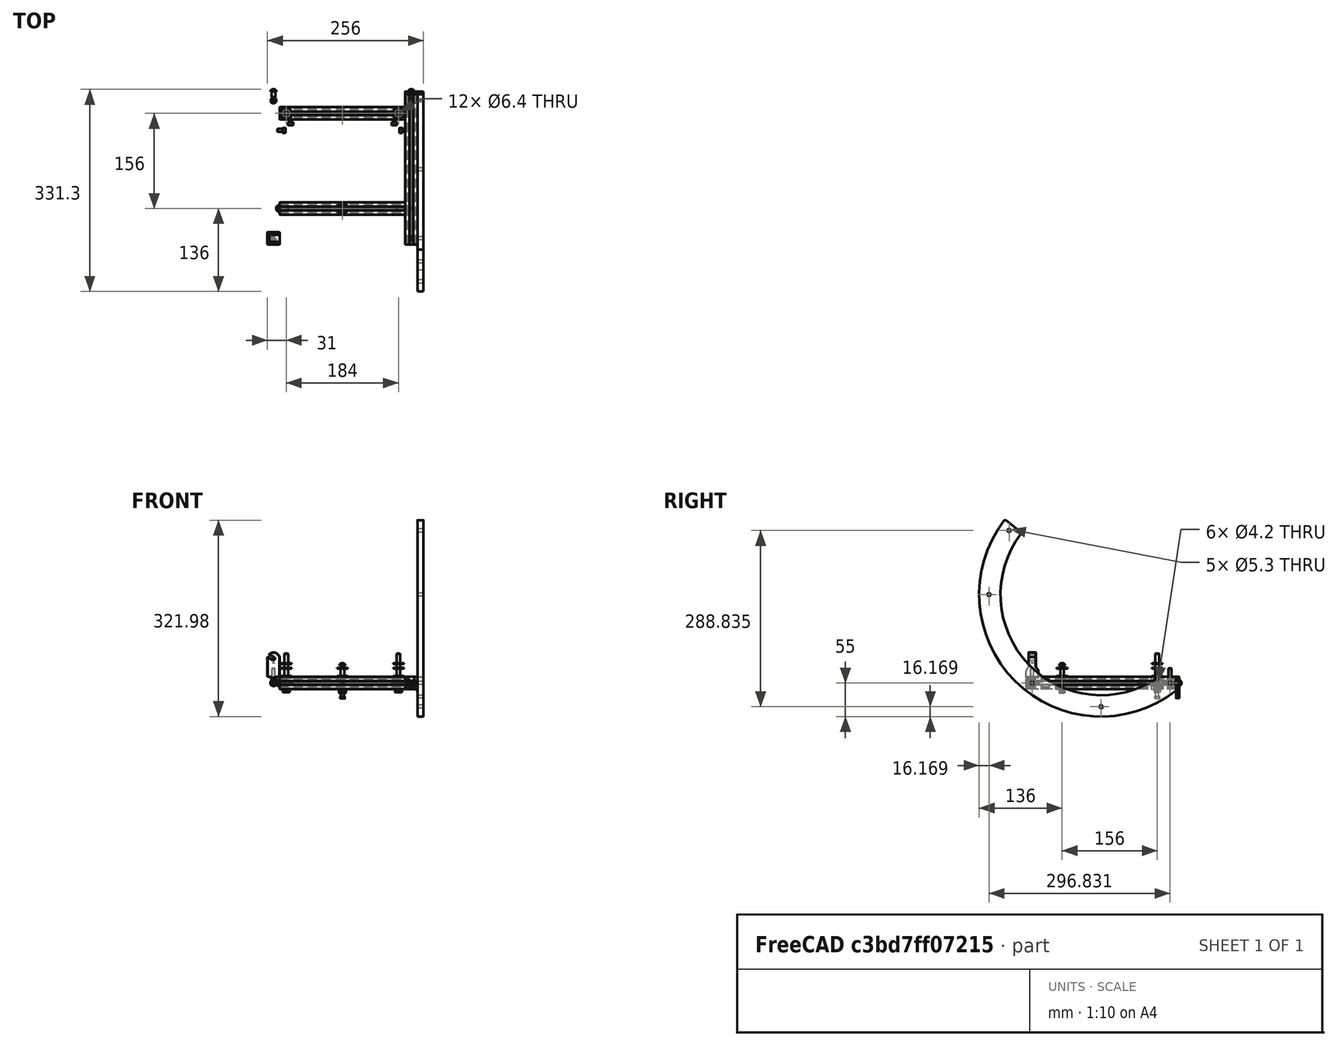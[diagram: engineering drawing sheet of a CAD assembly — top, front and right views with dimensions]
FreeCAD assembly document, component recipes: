
FREECAD ASSEMBLY — COMPONENT RECIPES ("Primary")

This assembly document has 7 components, labeled P0..P6 below (a component is one placed body or linked part). 6 of them carry a construction recipe — the FreeCAD feature program that regenerates the part from scratch, quoted from this document or its linked companion documents; the rest are supplied as boundary geometry only. No exploded tour is included for this assembly.
COMPONENT P0 — geometry summary ("EndStopper_M"; no construction recipe available for this part):
  bounding box: 35.0 x 30.0 x 10.0 mm
  tessellated surface: 1,512 triangles
  volume: 3951 mm^3 (38% of its bounding box)
COMPONENT P1 — recipe-attached ("RockerRail", modeled in this document).
Construction recipe (the document's own serialized feature program — sketch geometry with constraints, then the solid features built on it; lengths are millimeters unless a unit is written):

FEATURE [Sketcher::SketchObject] Sketch004  label="RockerRail_Base_Sketch"
  FullyConstrained = true
  MapMode = 5
  Placement = pos=(0,0,0) rot=(0.57735,0.57735,0.57735;2.0944rad)
  Support = -> [YZ_Plane011]
  expr: Constraints[12] = <<Common>>#<<Parameters>>.bolt_y - 10
  expr: Constraints[19] = <<Common>>#<<Parameters>>.pri_fillet
  expr: Constraints[1] = <<Common>>#<<Parameters>>.rail_dia
  expr: Constraints[35] = <<Common>>#<<Parameters>>.rail_dia - <<Common>>#<<Parameters>>.rail_height * 2
  expr: Constraints[36] = <<Common>>#<<Parameters>>.datum_lowercell - <<Common>>#<<Parameters>>.datum_rocker_z + 10
  expr: Constraints[40] = <<Common>>#<<Parameters>>.boxsize_y
  expr: Constraints[8] = <<Common>>#<<Parameters>>.boxsize_y
  sketch-geometry (16):
    g0: ArcOfCircle CenterX=0 CenterY=0 CenterZ=0 NormalX=0 NormalY=0 NormalZ=1 AngleXU=0 Radius=200 StartAngle=2.49187 EndAngle=5.36861
    g1: Circle CenterX=0 CenterY=0 CenterZ=0 NormalX=0 NormalY=0 NormalZ=1 AngleXU=0 Radius=165
    g2: LineSegment StartX=-155.722 StartY=121.453 StartZ=0 EndX=-132.064 EndY=103.001 EndZ=0
    g3: ArcOfCircle CenterX=0 CenterY=0 CenterZ=0 NormalX=0 NormalY=0 NormalZ=1 AngleXU=0 Radius=165 StartAngle=2.49413 EndAngle=5.32021
    g4: LineSegment StartX=95.6556 StartY=-135 StartZ=0 EndX=120.5 EndY=-135 EndZ=0
    g5: LineSegment StartX=123 StartY=-156.48 StartZ=0 EndX=123 EndY=-137.5 EndZ=0
    g6: LineSegment StartX=-123 StartY=-157.705 StartZ=0 EndX=123 EndY=-157.705 EndZ=0
    g7: LineSegment StartX=103 StartY=-157.705 StartZ=0 EndX=103 EndY=-128.903 EndZ=0
    g8: LineSegment StartX=0 StartY=0 StartZ=0 EndX=123 EndY=-135 EndZ=0
    g9: ArcOfCircle CenterX=120.5 CenterY=-137.5 CenterZ=0 NormalX=0 NormalY=0 NormalZ=1 AngleXU=0 Radius=2.5 StartAngle=-1.8e-15 EndAngle=1.5708
    g10: GeomPoint X=123 Y=-135 Z=0
    g11: ArcOfCircle CenterX=120.5 CenterY=-156.48 CenterZ=0 NormalX=0 NormalY=0 NormalZ=1 AngleXU=0 Radius=2.5 StartAngle=5.36861 EndAngle=6.28319
    g12: ArcOfCircle CenterX=-157.259 CenterY=119.481 CenterZ=0 NormalX=0 NormalY=0 NormalZ=1 AngleXU=0 Radius=2.5 StartAngle=0.90841 EndAngle=2.49187
    g13: ArcOfCircle CenterX=-133.601 CenterY=101.03 CenterZ=0 NormalX=0 NormalY=0 NormalZ=1 AngleXU=0 Radius=2.5 StartAngle=5.63573 EndAngle=7.1916
    g14: ArcOfCircle CenterX=95.6556 CenterY=-137.5 CenterZ=0 NormalX=0 NormalY=0 NormalZ=1 AngleXU=0 Radius=2.5 StartAngle=1.5708 EndAngle=2.17862
    g15: LineSegment StartX=-157.705 StartY=123 StartZ=0 EndX=-157.705 EndY=-123 EndZ=0
  constraints (42):
    c: Coincident(g0,g-1)
    c: Diameter(g0) = 400
    c: Coincident(g1,g0)
    c: PointOnObject(g0,g2)
    c: Coincident(g3,g0)
    c: Horizontal(g4)
    c: Vertical(g5)
    c: Symmetric(g6,g6,g-2)
    c: DistanceX(g6,g6) = 246
    c: PointOnObject(g7,g6)
    c: Vertical(g7)
    c: PointOnObject(g7,g1)
    c: DistanceX(g7) = 103
    c: Coincident(g8,g0)
    c: Coincident(g8,g10)
    c: PointOnObject(g10,g4)
    c: PointOnObject(g10,g5)
    c: Tangent(g4,g9) = 1.5708
    c: Tangent(g5,g9) = -1.5708
    c: Radius(g9) = 2.5
    c: Tangent(g5,g11) = -1.5708
    c: Tangent(g0,g11) = -1.5708
    c: Equal(g11,g9)
    c: PointOnObject(g6,g5)
    c: Tangent(g2,g12) = 1.5708
    c: Tangent(g0,g12) = -1.5708
    c: Equal(g12,g9)
    c: Tangent(g2,g13) = 1.5708
    c: Tangent(g3,g13) = 1.5708
    c: Equal(g12,g13)
    c: PointOnObject(g3,g1)
    c: Tangent(g4,g14) = 1.5708
    c: Tangent(g3,g14) = 1.5708
    c: Equal(g14,g9)
    c: PointOnObject(g6,g0)
    c: Diameter(g1) = 330
    c: DistanceY(g4) = -135
    c: PointOnObject(g15,g0)
    c: PointOnObject(g15,g0)
    c: Vertical(g15)
    c: DistanceY(g15,g15) = 246
    c: PointOnObject(g15,g2)
FEATURE [PartDesign::Plane] DatumPlane  label="DatumPlane_RockerBase_OuterFace"
  AttachmentOffset = pos=(0,0,5) rot=(0,0,1;0rad)
  Length = 386.928
  MapMode = 5
  Placement = pos=(5,-1.1e-15,1.1e-15) rot=(0.57735,0.57735,0.57735;2.0944rad)
  ResizeMode = 0
  Support = -> [YZ_Plane011]
  Width = 385.995
  expr: .AttachmentOffset.Base.z = <<Common>>#<<Parameters>>.rail_width / 2
FEATURE [PartDesign::Pad] Pad008  label="RockerRail_Base"
  Direction = (1,-2e-16,3e-16)
  Length = 10
  Length2 = 100
  Midplane = true
  Placement = pos=(0,0,0) rot=(0.57735,0.57735,0.57735;2.0944rad)
  Profile = -> Sketch004
  Type = 0
  expr: Length = <<Common>>#<<Parameters>>.rail_width
FEATURE [Sketcher::SketchObject] Sketch007  label="RockerRail_MountHoles_Sketch"
  ExternalGeometry = -> [Pad008]
  FullyConstrained = true
  MapMode = 5
  Placement = pos=(5,-1.1e-15,1.1e-15) rot=(0.57735,0.57735,0.57735;2.0944rad)
  Support = -> [DatumPlane]
  expr: Constraints[1] = <<Common>>#<<Parameters>>.bolt_y
  expr: Constraints[6] = <<Common>>#<<Parameters>>.datum_lowercell - <<Common>>#<<Parameters>>.datum_rocker_z
  sketch-geometry (8):
    g0: LineSegment StartX=-113 StartY=-145 StartZ=0 EndX=113 EndY=-145 EndZ=0
    g1: Circle CenterX=-113 CenterY=-145 CenterZ=0 NormalX=0 NormalY=0 NormalZ=1 AngleXU=0 Radius=2.5
    g2: Circle CenterX=113 CenterY=-145 CenterZ=0 NormalX=0 NormalY=0 NormalZ=1 AngleXU=0 Radius=2.5
    g3: Circle CenterX=0 CenterY=0 CenterZ=0 NormalX=0 NormalY=0 NormalZ=1 AngleXU=0 Radius=183.831
    g4: Circle CenterX=-150.891 CenterY=105.004 CenterZ=0 NormalX=0 NormalY=0 NormalZ=1 AngleXU=0 Radius=10
    g5: Circle CenterX=0 CenterY=-183.831 CenterZ=0 NormalX=0 NormalY=0 NormalZ=1 AngleXU=0 Radius=2.5
    g6: Circle CenterX=-183.831 CenterY=0 CenterZ=0 NormalX=0 NormalY=0 NormalZ=1 AngleXU=0 Radius=2.5
    g7: Circle CenterX=-150.891 CenterY=105.004 CenterZ=0 NormalX=0 NormalY=0 NormalZ=1 AngleXU=0 Radius=2.5
  constraints (22):
    c: Symmetric(g0,g0,g-2)
    c: DistanceX(g0) = 113
    c: Coincident(g1,g0)
    c: Coincident(g2,g0)
    c: Diameter(g2) = 5
    c: Equal(g2,g1)
    c: DistanceY(g2) = -145
    c: Distance(g-1,g1) = 183.831
    c: Coincident(g3,g-1)
    c: PointOnObject(g0,g3)
    c: PointOnObject(g4,g3)
    c: Tangent(g4,g-3)
    c: Radius(g4) = 10
    c: PointOnObject(g5,g-2)
    c: PointOnObject(g6,g3)
    c: Coincident(g7,g4)
    c: Equal(g7,g6)
    c: Equal(g6,g5)
    c: Equal(g5,g2)
    c: PointOnObject(g6,g-1)
    c: PointOnObject(g5,g3)
    c: Radius(g3) = 183.831
FEATURE [PartDesign::Hole] Hole003  label="RockerRail_MountHoles"
  BaseFeature = -> Pad008
  CustomThreadClearance = 0
  Depth = 25
  DepthType = 1
  Diameter = 5.3
  DrillForDepth = false
  DrillPoint = 1
  DrillPointAngle = 118
  HoleCutCountersinkAngle = 90
  HoleCutCustomValues = false
  HoleCutDepth = 0
  HoleCutDiameter = 12.2
  HoleCutType = 0
  ModelThread = false
  Placement = pos=(0,0,0) rot=(0.57735,0.57735,0.57735;2.0944rad)
  Profile = -> Sketch007
  Tapered = false
  TaperedAngle = 90
  ThreadClass = 0
  ThreadDepth = 23.5
  ThreadDepthType = 0
  ThreadDirection = 0
  ThreadFit = 1
  ThreadSize = 13
  ThreadType = 1
  Threaded = false
  UseCustomThreadClearance = false
FEATURE [PartDesign::CoordinateSystem] Local_CS024  label="LCS_RockerBolt_AS"
  AttacherType = Attacher::AttachEngine3D
  MapMode = 11
  Placement = pos=(-5,113,-145) rot=(0.707107,0,-0.707107;3.14159rad)
  Support = -> [Hole003]
FEATURE [PartDesign::CoordinateSystem] Local_CS026  label="LCS_RockerBolt_FS"
  AttacherType = Attacher::AttachEngine3D
  MapMode = 11
  Placement = pos=(-5,-113,-145) rot=(0.707107,0,-0.707107;3.14159rad)
  Support = -> [Hole003]
FEATURE [PartDesign::CoordinateSystem] Local_CS028  label="LCS_RockerBolt_AP"
  AttacherType = Attacher::AttachEngine3D
  MapMode = 11
  Placement = pos=(5,113,-145) rot=(0.707107,0,0.707107;3.14159rad)
  Support = -> [Hole003]
FEATURE [PartDesign::CoordinateSystem] Local_CS030  label="LCS_RockerBolt_FP"
  AttacherType = Attacher::AttachEngine3D
  MapMode = 11
  Placement = pos=(5,-113,-145) rot=(0.707107,0,0.707107;3.14159rad)
  Support = -> [Hole003]
FEATURE [PartDesign::Body] Body006  label="RockerRail"
  Group = -> [Sketch004,Sketch007,DatumPlane,Pad008,Hole003,Local_CS024,Local_CS026,Local_CS028,Local_CS030]
  Origin = -> Origin011
  Placement = pos=(128,0,83) rot=(0,0,1;0rad)
  Tip = -> Hole003
  expr: .Placement.Base.x = <<Common>>#<<Parameters>>.boxsize_x / 2 + <<Common>>#<<Parameters>>.rail_width / 2
  expr: .Placement.Base.z = <<Common>>#<<Parameters>>.datum_rocker_z
COMPONENT P2 — recipe-attached ("SideArmBase", modeled in this document).
Construction recipe (the document's own serialized feature program — sketch geometry with constraints, then the solid features built on it; lengths are millimeters unless a unit is written):

FEATURE [Sketcher::SketchObject] Sketch187  label="FrameBase_InnerCut_Sketch"
  AttachmentOffset = pos=(0,0,30) rot=(0,0,1;0rad)
  FullyConstrained = true
  MapMode = 5
  Placement = pos=(0,0,30) rot=(0,0,1;0rad)
  Support = -> [XY_Plane091]
  expr: .AttachmentOffset.Base.z = <<Common>>#<<Parameters>>.pri_braceriser
  sketch-geometry (1):
    g0: Circle CenterX=0 CenterY=0 CenterZ=0 NormalX=0 NormalY=0 NormalZ=1 AngleXU=0 Radius=4.75
  constraints (2):
    c: Diameter(g0) = 9.5
    c: Coincident(g0,g-1)
FEATURE [Sketcher::SketchObject] Sketch188  label="FrameBase_MountBolt_Sketch"
  AttachmentOffset = pos=(0,0,2) rot=(0,0,1;0rad)
  FullyConstrained = true
  MapMode = 5
  Placement = pos=(0,0,-2) rot=(0,1,0;3.14159rad)
  Support = -> [XY_Plane091]
  sketch-geometry (1):
    g0: Circle CenterX=0 CenterY=0 CenterZ=0 NormalX=0 NormalY=0 NormalZ=1 AngleXU=0 Radius=2.5
  constraints (2):
    c: Diameter(g0) = 5
    c: Coincident(g0,g-1)
FEATURE [Sketcher::SketchObject] Sketch189  label="FrameBase_Pivot_Sketch"
  FullyConstrained = true
  MapMode = 5
  Placement = pos=(0,0,0) rot=(1,0,0;1.5708rad)
  Support = -> [XZ_Plane092]
  expr: Constraints[10] = <<Common>>#<<Parameters>>.sec_sidebolt * 1.1
  expr: Constraints[4] = <<Common>>#<<Parameters>>.pri_bracepivotdia
  expr: Constraints[5] = <<Common>>#<<Parameters>>.pri_braceriser
  sketch-geometry (15):
    g0: LineSegment StartX=-10 StartY=0 StartZ=0 EndX=-10 EndY=30 EndZ=0
    g1: LineSegment StartX=10 StartY=0 StartZ=0 EndX=10 EndY=32.6795 EndZ=0
    g2: ArcOfCircle CenterX=0 CenterY=30 CenterZ=0 NormalX=0 NormalY=0 NormalZ=1 AngleXU=0 Radius=10 StartAngle=0.523599 EndAngle=2.39618
    g3: ArcOfCircle CenterX=0 CenterY=30 CenterZ=0 NormalX=0 NormalY=0 NormalZ=1 AngleXU=0 Radius=2.2 StartAngle=4.18879 EndAngle=7.33038
    g4: LineSegment StartX=-7.34808 StartY=36.7828 StartZ=0 EndX=1.1 EndY=31.9053 EndZ=0
    g5: LineSegment StartX=-1.1 StartY=28.0947 StartZ=0 EndX=-9.54808 EndY=32.9722 EndZ=0
    g6: LineSegment StartX=1.1 StartY=31.9053 StartZ=0 EndX=-1.1 EndY=28.0947 EndZ=0
    g7: ArcOfCircle CenterX=0 CenterY=30 CenterZ=0 NormalX=0 NormalY=0 NormalZ=1 AngleXU=0 Radius=10 StartAngle=2.83981 EndAngle=3.14159
    g8: LineSegment StartX=-10 StartY=30 StartZ=0 EndX=10 EndY=30 EndZ=0
    g9: LineSegment StartX=-10 StartY=0 StartZ=0 EndX=-3 EndY=0 EndZ=0
    g10: LineSegment StartX=10 StartY=0 StartZ=0 EndX=3 EndY=0 EndZ=0
    g11: LineSegment StartX=3 StartY=0 StartZ=0 EndX=1.8453 EndY=-2 EndZ=0
    g12: LineSegment StartX=1.8453 StartY=-2 StartZ=0 EndX=-3 EndY=-2 EndZ=0
    g13: LineSegment StartX=-3 StartY=-2 StartZ=0 EndX=-3 EndY=0 EndZ=0
    g14: LineSegment StartX=8.66025 StartY=35 StartZ=0 EndX=10 EndY=32.6795 EndZ=0
  constraints (42):
    c: PointOnObject(g1,g-1)
    c: Vertical(g0)
    c: Vertical(g1)
    c: PointOnObject(g2,g-2)
    c: Diameter(g2) = 20
    c: DistanceY(g2) = 30
    c: Coincident(g3,g2)
    c: Coincident(g4,g2)
    c: Coincident(g4,g3)
    c: Coincident(g5,g3)
    c: Diameter(g3) = 4.4
    c: Symmetric(g1,g0,g-2)
    c: Coincident(g6,g3)
    c: Coincident(g6,g3)
    c: PointOnObject(g2,g6)
    c: Parallel(g5,g4)
    c: Coincident(g7,g2)
    c: Coincident(g7,g5)
    c: Coincident(g7,g0)
    c: Coincident(g8,g0)
    c: PointOnObject(g2,g8)
    c: Perpendicular(g4,g6)
    c: Horizontal(g8)
    c: Angle(g4,g8) = 0.523599
    c: Coincident(g9,g0)
    c: Horizontal(g9)
    c: Coincident(g10,g1)
    c: Coincident(g11,g10)
    c: Coincident(g12,g11)
    c: Horizontal(g12)
    c: Coincident(g13,g12)
    c: Coincident(g13,g9)
    c: Vertical(g13)
    c: DistanceX(g9,g10) = 6
    c: Symmetric(g10,g9,g-2)
    c: DistanceY(g13,g13) = 2
    c: Angle(g11,g10) = 2.0944
    c: PointOnObject(g8,g1)
    c: DistanceX(g1) = 10
    c: Coincident(g14,g1)
    c: Tangent(g14,g2) = 1.5708
    c: Angle(g14,g1) = 2.61799
FEATURE [Sketcher::SketchObject] Sketch190  label="FrameBase_Hinge_Sketch"
  FullyConstrained = true
  MapMode = 5
  Placement = pos=(0,0,0) rot=(0.57735,0.57735,0.57735;2.0944rad)
  Support = -> [YZ_Plane092]
  expr: Constraints[22] = <<Common>>#<<Parameters>>.pri_braceriser + <<Common>>#<<Parameters>>.pri_bracepivotdia / 2
  expr: Constraints[23] = <<Common>>#<<Parameters>>.pri_braceriser + <<Common>>#<<Parameters>>.pri_bracepivotdia / 2 + 1
  expr: Constraints[26] = <<Common>>#<<Parameters>>.pri_braceriser - <<Common>>#<<Parameters>>.pri_bracepivotdia / 2 - <<Common>>#<<Parameters>>.sec_fthick / 2
  expr: Constraints[35] = <<Common>>#<<Parameters>>.sec_fthick + 1
  expr: Constraints[47] = <<Common>>#<<Parameters>>.sec_fthick * 2
  expr: Constraints[4] = <<Common>>#<<Parameters>>.sec_fthick
  sketch-geometry (20):
    g0: LineSegment StartX=6 StartY=18.5 StartZ=0 EndX=6 EndY=40 EndZ=0
    g1: LineSegment StartX=6 StartY=40 StartZ=0 EndX=-6 EndY=40 EndZ=0
    g2: LineSegment StartX=-6 StartY=40 StartZ=0 EndX=-6 EndY=18.5 EndZ=0
    g3: LineSegment StartX=-10 StartY=3 StartZ=0 EndX=10 EndY=3 EndZ=0
    g4: LineSegment StartX=10 StartY=9.55573 StartZ=0 EndX=10 EndY=3 EndZ=0
    g5: LineSegment StartX=-10 StartY=9.55573 StartZ=0 EndX=-10 EndY=3 EndZ=0
    g6: LineSegment StartX=10 StartY=3 StartZ=0 EndX=11 EndY=3 EndZ=0
    g7: LineSegment StartX=11 StartY=3 StartZ=0 EndX=11 EndY=41 EndZ=0
    g8: LineSegment StartX=-10 StartY=3 StartZ=0 EndX=-11 EndY=3 EndZ=0
    g9: LineSegment StartX=-11 StartY=3 StartZ=0 EndX=-11 EndY=41 EndZ=0
    g10: LineSegment StartX=-11 StartY=41 StartZ=0 EndX=11 EndY=41 EndZ=0
    g11: LineSegment StartX=-6 StartY=18.5 StartZ=0 EndX=6 EndY=18.5 EndZ=0
    g12: LineSegment StartX=6 StartY=18.5 StartZ=0 EndX=10 EndY=18.5 EndZ=0
    g13: LineSegment StartX=-6 StartY=18.5 StartZ=0 EndX=-10 EndY=18.5 EndZ=0
    g14: ArcOfCircle CenterX=-12 CenterY=18.5 CenterZ=0 NormalX=0 NormalY=0 NormalZ=1 AngleXU=0 Radius=6 StartAngle=5.44212 EndAngle=6.28319
    g15: ArcOfCircle CenterX=-4 CenterY=9.55573 CenterZ=0 NormalX=0 NormalY=0 NormalZ=1 AngleXU=0 Radius=6 StartAngle=2.30052 EndAngle=3.14159
    g16: ArcOfCircle CenterX=12 CenterY=18.5 CenterZ=0 NormalX=0 NormalY=0 NormalZ=1 AngleXU=0 Radius=6 StartAngle=3.14159 EndAngle=3.98266
    g17: ArcOfCircle CenterX=4 CenterY=9.55573 CenterZ=0 NormalX=0 NormalY=0 NormalZ=1 AngleXU=0 Radius=6 StartAngle=1e-16 EndAngle=0.841069
    g18: LineSegment StartX=-12 StartY=18.5 StartZ=0 EndX=-4 EndY=9.55573 EndZ=0
    g19: LineSegment StartX=4 StartY=9.55573 StartZ=0 EndX=12 EndY=18.5 EndZ=0
  constraints (55):
    c: Coincident(g1,g0)
    c: Coincident(g2,g1)
    c: Vertical(g2)
    c: Symmetric(g3,g3,g-2)
    c: DistanceY(g-1,g3) = 3
    c: DistanceX(g3,g3) = 20
    c: Vertical(g0)
    c: Symmetric(g1,g0,g-2)
    c: Coincident(g4,g3)
    c: Coincident(g5,g3)
    c: Coincident(g6,g4)
    c: Coincident(g7,g6)
    c: Vertical(g7)
    c: Coincident(g8,g5)
    c: Horizontal(g8)
    c: Coincident(g9,g8)
    c: Vertical(g9)
    c: Coincident(g10,g9)
    c: Coincident(g10,g7)
    c: Symmetric(g7,g9,g-2)
    c: DistanceX(g6,g6) = 1
    c: Horizontal(g6)
    c: DistanceY(g1) = 40
    c: DistanceY(g7) = 41
    c: Coincident(g11,g2)
    c: Horizontal(g11)
    c: DistanceY(g2) = 18.5
    c: Vertical(g4)
    c: Vertical(g5)
    c: Coincident(g12,g0)
    c: Horizontal(g12)
    c: Coincident(g13,g2)
    c: Horizontal(g13)
    c: PointOnObject(g13,g5)
    c: PointOnObject(g12,g4)
    c: DistanceX(g12,g12) = 4
    c: Coincident(g11,g0)
    c: Coincident(g14,g2)
    c: Coincident(g15,g14)
    c: Coincident(g16,g0)
    c: Coincident(g17,g16)
    c: Coincident(g18,g14)
    c: Coincident(g18,g15)
    c: Coincident(g19,g17)
    c: Coincident(g19,g16)
    c: PointOnObject(g14,g18)
    c: PointOnObject(g16,g19)
    c: Radius(g16) = 6
    c: Equal(g16,g17)
    c: Equal(g16,g14)
    c: Equal(g16,g15)
    c: PointOnObject(g14,g13)
    c: PointOnObject(g16,g12)
    c: Tangent(g15,g5) = -1.5708
    c: Tangent(g17,g4) = 1.5708
FEATURE [PartDesign::CoordinateSystem] Local_CS259  label="LCS_FrameBase_Pivot"
  AttacherType = Attacher::AttachEngine3D
  AttachmentOffset = pos=(0,0,0) rot=(-0.935113,-0.250563,0.250563;1.63783rad)
  MapMode = 11
  Placement = pos=(0,-6.7e-15,30) rot=(0,0,1;0rad)
  Support = -> [Sketch189]
FEATURE [PartDesign::Pad] Pad059  label="FrameBase_Pivot"
  Direction = (0,-1,-2e-16)
  Length = 20
  Length2 = 100
  Midplane = true
  Placement = pos=(0,0,0) rot=(1,0,0;1.5708rad)
  Profile = -> Sketch189
  Type = 0
  expr: Length = 20
FEATURE [PartDesign::Pocket] Pocket157  label="FrameBase_Hinge"
  BaseFeature = -> Pad059
  Direction = (-1,2e-16,-3e-16)
  Length = 5
  Length2 = 100
  Midplane = true
  Placement = pos=(0,0,0) rot=(1,0,0;1.5708rad)
  Profile = -> Sketch190
  Type = 1
FEATURE [PartDesign::Plane] DatumPlane055  label="DatumPlane_FrameBase_Pivot"
  AttachmentOffset = pos=(0,30,10) rot=(0,0,1;0rad)
  Length = 61.4018
  MapMode = 5
  Placement = pos=(0,-10,30) rot=(1,0,0;1.5708rad)
  ResizeMode = 0
  Support = -> [XZ_Plane092]
  Width = 76.4018
  expr: .AttachmentOffset.Base.y = <<Common>>#<<Parameters>>.pri_braceriser
  expr: .AttachmentOffset.Base.z = <<Common>>#<<Parameters>>.pri_bracepivotdia / 2
FEATURE [Sketcher::SketchObject] Sketch240  label="FrameBase_ClampNut_Sketch"
  AttachmentOffset = pos=(0,0,3) rot=(0,0,1;0rad)
  FullyConstrained = true
  MapMode = 5
  Placement = pos=(0,-13,30) rot=(1,0,0;1.5708rad)
  Support = -> [DatumPlane055]
  sketch-geometry (7):
    g0: LineSegment StartX=0 StartY=4.15692 StartZ=0 EndX=-3.6 EndY=2.07846 EndZ=0
    g1: LineSegment StartX=-3.6 StartY=2.07846 StartZ=0 EndX=-3.6 EndY=-2.07846 EndZ=0
    g2: LineSegment StartX=-3.6 StartY=-2.07846 StartZ=0 EndX=9e-16 EndY=-4.15692 EndZ=0
    g3: LineSegment StartX=9e-16 StartY=-4.15692 StartZ=0 EndX=3.6 EndY=-2.07846 EndZ=0
    g4: LineSegment StartX=3.6 StartY=-2.07846 StartZ=0 EndX=3.6 EndY=2.07846 EndZ=0
    g5: LineSegment StartX=3.6 StartY=2.07846 StartZ=0 EndX=0 EndY=4.15692 EndZ=0
    g6: Circle CenterX=0 CenterY=0 CenterZ=0 NormalX=0 NormalY=0 NormalZ=1 AngleXU=0 Radius=4.15692
  constraints (16):
    c: Coincident(g0,g1)
    c: Coincident(g1,g2)
    c: Coincident(g2,g3)
    c: Coincident(g3,g4)
    c: Coincident(g4,g5)
    c: Coincident(g5,g0)
    c: Equal(g0, g1-g5) x5
    c: PointOnObject(g0,g6)
    c: PointOnObject(g1,g6)
    c: PointOnObject(g2,g6)
    c: PointOnObject(g3,g6)
    c: PointOnObject(g4,g6)
    c: PointOnObject(g5,g6)
    c: Coincident(g6,g-1)
    c: PointOnObject(g5,g-2)
    c: DistanceX(g0,g4) = 7.2
FEATURE [PartDesign::Hole] Hole055  label="FrameBase_MountBolt"
  BaseFeature = -> Pocket157
  CustomThreadClearance = 0
  Depth = 25
  DepthType = 0
  Diameter = 4.2
  DrillForDepth = false
  DrillPoint = 1
  DrillPointAngle = 118
  HoleCutCountersinkAngle = 90
  HoleCutCustomValues = false
  HoleCutDepth = 0
  HoleCutDiameter = 6.1
  HoleCutType = 0
  ModelThread = false
  Placement = pos=(0,0,0) rot=(1,0,0;1.5708rad)
  Profile = -> Sketch188
  Tapered = false
  TaperedAngle = 90
  ThreadClass = 0
  ThreadDepth = 23.5
  ThreadDepthType = 0
  ThreadDirection = 0
  ThreadFit = 0
  ThreadSize = 13
  ThreadType = 1
  Threaded = true
  UseCustomThreadClearance = false
FEATURE [PartDesign::CoordinateSystem] Local_CS321  label="FrameBase_Pivot_Tilt"
  AttacherType = Attacher::AttachEngine3D
  AttachmentOffset = pos=(0,0,0) rot=(1,0,0;0.440587rad)
  MapMode = 5
  Placement = pos=(0,-6.7e-15,30) rot=(1,0,0;0.440587rad)
  Support = -> [Local_CS259]
  expr: .AttachmentOffset.Rotation.Roll = <<Common>>#<<Parameters>>.pri_bracetilt
FEATURE [Sketcher::SketchObject] Sketch  label="FrameBase_NutCut_Sketch"
  FullyConstrained = true
  MapMode = 5
  Placement = pos=(0,0,0) rot=(0.57735,0.57735,0.57735;2.0944rad)
  Support = -> [YZ_Plane092]
  sketch-geometry (4):
    g0: LineSegment StartX=-5 StartY=-5 StartZ=0 EndX=5 EndY=-5 EndZ=0
    g1: LineSegment StartX=5 StartY=-5 StartZ=0 EndX=5 EndY=0 EndZ=0
    g2: LineSegment StartX=5 StartY=0 StartZ=0 EndX=-5 EndY=0 EndZ=0
    g3: LineSegment StartX=-5 StartY=0 StartZ=0 EndX=-5 EndY=-5 EndZ=0
  constraints (11):
    c: Coincident(g0,g1)
    c: Coincident(g1,g2)
    c: Coincident(g2,g3)
    c: Coincident(g3,g0)
    c: Horizontal(g0)
    c: Vertical(g1)
    c: Vertical(g3)
    c: PointOnObject(g1,g-1)
    c: Symmetric(g2,g1,g-2)
    c: DistanceX(g0,g0) = 10
    c: DistanceY(g1,g1) = 5
FEATURE [PartDesign::Pocket] Pocket  label="FrameBase_NutCut"
  BaseFeature = -> Hole055
  Direction = (-1,2e-16,-3e-16)
  Length = 6
  Length2 = 5
  Midplane = true
  Placement = pos=(0,0,0) rot=(1,0,0;1.5708rad)
  Profile = -> Sketch
  ReferenceAxis = -> Sketch [N_Axis]
  Type = 0
FEATURE [PartDesign::CoordinateSystem] Local_CS257  label="LCS_FrameBase_Base"
  AttacherType = Attacher::AttachEngine3D
  AttachmentOffset = pos=(0,0,0) rot=(0,0,-1;1.5708rad)
  MapMode = 11
  Placement = pos=(0,0,0) rot=(0,1,0;3.14159rad)
  Support = -> [Pocket]
FEATURE [PartDesign::Chamfer] Chamfer001  label="FrameBase_Chamfer"
  Angle = 45
  Base = -> Pocket [Edge26,Edge24,Edge22,Edge20,Edge18,Edge65,Edge49,Edge46,Edge55,Edge44,Edge38,Edge12,Edge1,Edge2,Edge3,Edge4,Edge5,Edge33,Edge34,Edge7,Edge8,Edge9,Edge10,Edge11,Edge28,Edge27,Edge29,Edge43,Edge36,Edge37,Edge71,Edge35,Edge30,Edge31,Edge32,Edge42,Edge41,Edge40]
  BaseFeature = -> Pocket
  ChamferType = 0
  FlipDirection = false
  Placement = pos=(0,0,0) rot=(1,0,0;1.5708rad)
  Size = 0.4
  Size2 = 1
  SupportTransform = false
  UseAllEdges = false
FEATURE [PartDesign::Body] Body022039  label="SideArmBase"
  Group = -> [Sketch187,Sketch188,Sketch189,Sketch190,Local_CS257,Local_CS259,Sketch240,Pad059,Pocket157,DatumPlane055,Hole055,Local_CS321,Sketch,Pocket,Chamfer001]
  Origin = -> Origin092
  Placement = pos=(-113,-113,-52) rot=(0,0,1;0rad)
  Tip = -> Chamfer001
  expr: .Placement.Base.x = -<<Common>>#<<Parameters>>.bolt_x
  expr: .Placement.Base.y = -<<Common>>#<<Parameters>>.bolt_y
  expr: .Placement.Base.z = <<Common>>#<<Parameters>>.datum_uppercell - <<Common>>#<<Parameters>>.pri_cellfloat
COMPONENT P3 — recipe-attached ("EndStopper", modeled in this document).
Construction recipe (the document's own serialized feature program — sketch geometry with constraints, then the solid features built on it; lengths are millimeters unless a unit is written):

FEATURE [Sketcher::SketchObject] Sketch211  label="EndStopper_Base_Sketch"
  FullyConstrained = true
  MapMode = 5
  Placement = pos=(0,0,0) rot=(1,0,0;1.5708rad)
  Support = -> [XZ_Plane099]
  sketch-geometry (19):
    g0: LineSegment StartX=9 StartY=10 StartZ=0 EndX=-19 EndY=10 EndZ=0
    g1: LineSegment StartX=-20 StartY=9 StartZ=0 EndX=-20 EndY=-24 EndZ=0
    g2: LineSegment StartX=-19 StartY=-25 StartZ=0 EndX=-11 EndY=-25 EndZ=0
    g3: LineSegment StartX=-10 StartY=-24 StartZ=0 EndX=-10 EndY=-15 EndZ=0
    g4: LineSegment StartX=-5 StartY=-10 StartZ=0 EndX=9 EndY=-10 EndZ=0
    g5: LineSegment StartX=10 StartY=9 StartZ=0 EndX=10 EndY=-9 EndZ=0
    g6: ArcOfCircle CenterX=-19 CenterY=9 CenterZ=0 NormalX=0 NormalY=0 NormalZ=1 AngleXU=0 Radius=1 StartAngle=1.5708 EndAngle=3.14159
    g7: ArcOfCircle CenterX=9 CenterY=9 CenterZ=0 NormalX=0 NormalY=0 NormalZ=1 AngleXU=0 Radius=1 StartAngle=-9e-16 EndAngle=1.5708
    g8: ArcOfCircle CenterX=9 CenterY=-9 CenterZ=0 NormalX=0 NormalY=0 NormalZ=1 AngleXU=0 Radius=1 StartAngle=4.71239 EndAngle=6.28319
    g9: ArcOfCircle CenterX=-5 CenterY=-15 CenterZ=0 NormalX=0 NormalY=0 NormalZ=1 AngleXU=0 Radius=5 StartAngle=1.5708 EndAngle=3.14159
    g10: ArcOfCircle CenterX=-11 CenterY=-24 CenterZ=0 NormalX=0 NormalY=0 NormalZ=1 AngleXU=0 Radius=1 StartAngle=4.71239 EndAngle=6.28319
    g11: ArcOfCircle CenterX=-19 CenterY=-24 CenterZ=0 NormalX=0 NormalY=0 NormalZ=1 AngleXU=0 Radius=1 StartAngle=3.14159 EndAngle=4.71239
    g12: LineSegment StartX=-20 StartY=-24 StartZ=0 EndX=-10 EndY=-24 EndZ=0
    g13: LineSegment StartX=-20 StartY=9 StartZ=0 EndX=10 EndY=9 EndZ=0
    g14: LineSegment StartX=9 StartY=-10 StartZ=0 EndX=9 EndY=10 EndZ=0
    g15: LineSegment StartX=-19 StartY=10 StartZ=0 EndX=-19 EndY=-25 EndZ=0
    g16: LineSegment StartX=-10 StartY=-15 StartZ=0 EndX=-5 EndY=-15 EndZ=0
    g17: LineSegment StartX=-5 StartY=-15 StartZ=0 EndX=-5 EndY=-10 EndZ=0
    g18: Circle CenterX=0 CenterY=0 CenterZ=0 NormalX=0 NormalY=0 NormalZ=1 AngleXU=0 Radius=3.25
  constraints (56):
    c: Horizontal(g0)
    c: Vertical(g1)
    c: Horizontal(g2)
    c: Vertical(g3)
    c: Horizontal(g4)
    c: Vertical(g5)
    c: Coincident(g6,g0)
    c: Coincident(g7,g0)
    c: Coincident(g7,g5)
    c: Coincident(g8,g5)
    c: Coincident(g8,g4)
    c: Coincident(g9,g4)
    c: Coincident(g9,g3)
    c: Coincident(g10,g3)
    c: Coincident(g10,g2)
    c: Coincident(g11,g1)
    c: Coincident(g11,g2)
    c: Coincident(g1,g6)
    c: Equal(g7,g6)
    c: Equal(g7,g8)
    c: Equal(g7,g10)
    c: Equal(g7,g11)
    c: Radius(g7) = 1
    c: DistanceY(g0) = 10
    c: DistanceX(g5) = 10
    c: DistanceX(g1) = -20
    c: DistanceY(g4) = -10
    c: DistanceX(g3) = -10
    c: DistanceY(g2) = -25
    c: Coincident(g12,g1)
    c: Coincident(g12,g3)
    c: Horizontal(g12)
    c: PointOnObject(g11,g12)
    c: PointOnObject(g10,g12)
    c: Coincident(g13,g1)
    c: Coincident(g13,g5)
    c: Horizontal(g13)
    c: Coincident(g14,g4)
    c: Coincident(g14,g0)
    c: Vertical(g14)
    c: PointOnObject(g6,g13)
    c: PointOnObject(g7,g14)
    c: PointOnObject(g7,g13)
    c: PointOnObject(g8,g14)
    c: Coincident(g15,g0)
    c: Coincident(g15,g2)
    c: Vertical(g15)
    c: Coincident(g16,g3)
    c: Coincident(g16,g9)
    c: Coincident(g17,g9)
    c: Coincident(g17,g4)
    c: Horizontal(g16)
    c: Vertical(g17)
    c: Coincident(g18,g-1)
    c: Diameter(g18) = 6.5
    c: Radius(g9) = 5
FEATURE [PartDesign::Pad] Pad055  label="EndStopper_Base"
  Direction = (0,-1,-2e-16)
  Length = 5
  Length2 = 10
  Placement = pos=(0,0,0) rot=(1,0,0;1.5708rad)
  Profile = -> Sketch211
  Reversed = true
  Type = 0
FEATURE [Sketcher::SketchObject] Sketch212  label="EndStopper_Tab_Sketch"
  FullyConstrained = true
  MapMode = 5
  Placement = pos=(0,0,0) rot=(1,0,0;1.5708rad)
  Support = -> [XZ_Plane099]
  sketch-geometry (12):
    g0: LineSegment StartX=-10 StartY=3 StartZ=0 EndX=-6 EndY=3 EndZ=0
    g1: LineSegment StartX=-6 StartY=3 StartZ=0 EndX=-6 EndY=-3 EndZ=0
    g2: LineSegment StartX=-6 StartY=-3 StartZ=0 EndX=-10 EndY=-3 EndZ=0
    g3: LineSegment StartX=-10 StartY=-3 StartZ=0 EndX=-10 EndY=3 EndZ=0
    g4: LineSegment StartX=10 StartY=3 StartZ=0 EndX=6 EndY=3 EndZ=0
    g5: LineSegment StartX=6 StartY=3 StartZ=0 EndX=6 EndY=-3 EndZ=0
    g6: LineSegment StartX=6 StartY=-3 StartZ=0 EndX=10 EndY=-3 EndZ=0
    g7: LineSegment StartX=10 StartY=-3 StartZ=0 EndX=10 EndY=3 EndZ=0
    g8: LineSegment StartX=-3 StartY=-10 StartZ=0 EndX=3 EndY=-10 EndZ=0
    g9: LineSegment StartX=3 StartY=-10 StartZ=0 EndX=3 EndY=-6 EndZ=0
    g10: LineSegment StartX=3 StartY=-6 StartZ=0 EndX=-3 EndY=-6 EndZ=0
    g11: LineSegment StartX=-3 StartY=-6 StartZ=0 EndX=-3 EndY=-10 EndZ=0
  constraints (33):
    c: Coincident(g0,g1)
    c: Coincident(g1,g2)
    c: Coincident(g2,g3)
    c: Coincident(g3,g0)
    c: Horizontal(g0)
    c: Horizontal(g2)
    c: Vertical(g3)
    c: Coincident(g4,g5)
    c: Coincident(g5,g6)
    c: Coincident(g6,g7)
    c: Coincident(g7,g4)
    c: Horizontal(g4)
    c: Horizontal(g6)
    c: Vertical(g5)
    c: Vertical(g7)
    c: Coincident(g8,g9)
    c: Coincident(g9,g10)
    c: Coincident(g10,g11)
    c: Coincident(g11,g8)
    c: Horizontal(g8)
    c: Vertical(g9)
    c: Vertical(g11)
    c: Equal(g7,g8)
    c: Equal(g8,g3)
    c: DistanceX(g8,g8) = 6
    c: Equal(g0,g11)
    c: Equal(g11,g6)
    c: DistanceX(g6,g6) = 4
    c: DistanceX(g0) = -10
    c: Symmetric(g4,g0,g-2)
    c: Symmetric(g10,g9,g-2)
    c: DistanceY(g8,g-1) = 10
    c: Symmetric(g1,g0,g-1)
FEATURE [PartDesign::Pad] Pad056  label="EndStopper_Tab"
  BaseFeature = -> Pad055
  Direction = (0,-1,-2e-16)
  Length = 5
  Length2 = 10
  Placement = pos=(0,0,0) rot=(1,0,0;1.5708rad)
  Profile = -> Sketch212
  Type = 0
FEATURE [PartDesign::CoordinateSystem] Local_CS261  label="LCS_EndStopper_Mount"
  AttacherType = Attacher::AttachEngine3D
  MapMode = 11
  Placement = pos=(0,0,0) rot=(0.57735,-0.57735,0.57735;2.0944rad)
  Support = -> [Pad056]
FEATURE [PartDesign::Chamfer] Chamfer  label="EndStopper_Chamfer"
  Angle = 45
  Base = -> Pad056 [Face5]
  BaseFeature = -> Pad056
  ChamferType = 0
  FlipDirection = false
  Placement = pos=(0,0,0) rot=(1,0,0;1.5708rad)
  Size = 0.45
  Size2 = 1
  SupportTransform = false
  UseAllEdges = false
FEATURE [PartDesign::Body] Body022046  label="EndStopper"
  Group = -> [Sketch211,Pad055,Sketch212,Pad056,Local_CS261,Chamfer]
  Origin = -> Origin099
  Placement = pos=(-113,123,-62) rot=(0,0,1;0rad)
  Tip = -> Chamfer
  expr: .Placement.Base.x = -<<Common>>#<<Parameters>>.bolt_x
  expr: .Placement.Base.y = <<Common>>#<<Parameters>>.boxsize_y / 2
  expr: .Placement.Base.z = <<Common>>#<<Parameters>>.datum_uppercell - <<Common>>#<<Parameters>>.pri_cellfloat - 10
COMPONENT P4 — recipe-attached ("Frame_PS", modeled in this document).
Construction recipe (the document's own serialized feature program — sketch geometry with constraints, then the solid features built on it; lengths are millimeters unless a unit is written):

FEATURE [Sketcher::SketchObject] Sketch044  label="Frame_P_Sketch"
  FullyConstrained = true
  MapMode = 5
  Placement = pos=(0,0,0) rot=(1,0,0;1.5708rad)
  Support = -> [XZ_Plane035]
  sketch-geometry (75):
    g0: LineSegment StartX=3 StartY=10 StartZ=0 EndX=3 EndY=8 EndZ=0
    g1: LineSegment StartX=3 StartY=8 StartZ=0 EndX=6 EndY=8 EndZ=0
    g2: LineSegment StartX=2.58579 StartY=4 StartZ=0 EndX=-2.58579 EndY=4 EndZ=0
    g3: LineSegment StartX=-6 StartY=8 StartZ=0 EndX=-3 EndY=8 EndZ=0
    g4: LineSegment StartX=-3 StartY=8 StartZ=0 EndX=-3 EndY=10 EndZ=0
    g5: Circle CenterX=0 CenterY=0 CenterZ=0 NormalX=0 NormalY=0 NormalZ=1 AngleXU=0 Radius=2.1
    g6: LineSegment StartX=-10 StartY=3 StartZ=0 EndX=-8 EndY=3 EndZ=0
    g7: LineSegment StartX=-8 StartY=3 StartZ=0 EndX=-8 EndY=6 EndZ=0
    g8: LineSegment StartX=-4 StartY=2.58579 StartZ=0 EndX=-4 EndY=-2.58579 EndZ=0
    g9: LineSegment StartX=-8 StartY=-6 StartZ=0 EndX=-8 EndY=-3 EndZ=0
    g10: LineSegment StartX=-8 StartY=-3 StartZ=0 EndX=-10 EndY=-3 EndZ=0
    g11: LineSegment StartX=-3 StartY=-10 StartZ=0 EndX=-3 EndY=-8 EndZ=0
    g12: LineSegment StartX=-3 StartY=-8 StartZ=0 EndX=-6 EndY=-8 EndZ=0
    g13: LineSegment StartX=-2.58579 StartY=-4 StartZ=0 EndX=2.58579 EndY=-4 EndZ=0
    g14: LineSegment StartX=6 StartY=-8 StartZ=0 EndX=3 EndY=-8 EndZ=0
    g15: LineSegment StartX=3 StartY=-8 StartZ=0 EndX=3 EndY=-10 EndZ=0
    g16: LineSegment StartX=10 StartY=-3 StartZ=0 EndX=8 EndY=-3 EndZ=0
    g17: LineSegment StartX=8 StartY=-3 StartZ=0 EndX=8 EndY=-6 EndZ=0
    g18: LineSegment StartX=8 StartY=-6 StartZ=0 EndX=7.41421 EndY=-6 EndZ=0
    g19: LineSegment StartX=7.41421 StartY=-6 StartZ=0 EndX=4 EndY=-2.58579 EndZ=0
    g20: LineSegment StartX=4 StartY=-2.58579 StartZ=0 EndX=4 EndY=2.58579 EndZ=0
    g21: LineSegment StartX=4 StartY=2.58579 StartZ=0 EndX=7.41421 EndY=6 EndZ=0
    g22: LineSegment StartX=7.41421 StartY=6 StartZ=0 EndX=8 EndY=6 EndZ=0
    g23: LineSegment StartX=8 StartY=6 StartZ=0 EndX=8 EndY=3 EndZ=0
    g24: LineSegment StartX=8 StartY=3 StartZ=0 EndX=10 EndY=3 EndZ=0
    g25: LineSegment StartX=6 StartY=8 StartZ=0 EndX=6 EndY=7.41421 EndZ=0
    g26: LineSegment StartX=6 StartY=7.41421 StartZ=0 EndX=2.58579 EndY=4 EndZ=0
    g27: LineSegment StartX=-2.58579 StartY=4 StartZ=0 EndX=-6 EndY=7.41421 EndZ=0
    g28: LineSegment StartX=-6 StartY=7.41421 StartZ=0 EndX=-6 EndY=8 EndZ=0
    g29: LineSegment StartX=-8 StartY=6 StartZ=0 EndX=-7.41421 EndY=6 EndZ=0
    g30: LineSegment StartX=-7.41421 StartY=6 StartZ=0 EndX=-4 EndY=2.58579 EndZ=0
    g31: LineSegment StartX=-4 StartY=-2.58579 StartZ=0 EndX=-7.41421 EndY=-6 EndZ=0
    g32: LineSegment StartX=-7.41421 StartY=-6 StartZ=0 EndX=-8 EndY=-6 EndZ=0
    g33: LineSegment StartX=-2.58579 StartY=-4 StartZ=0 EndX=-6 EndY=-7.41421 EndZ=0
    g34: LineSegment StartX=-6 StartY=-7.41421 StartZ=0 EndX=-6 EndY=-8 EndZ=0
    g35: LineSegment StartX=2.58579 StartY=-4 StartZ=0 EndX=6 EndY=-7.41421 EndZ=0
    g36: LineSegment StartX=6 StartY=-7.41421 StartZ=0 EndX=6 EndY=-8 EndZ=0
    g37: LineSegment StartX=-4 StartY=2.58579 StartZ=0 EndX=-2.58579 EndY=4 EndZ=0
    g38: LineSegment StartX=-7.41421 StartY=7.41421 StartZ=0 EndX=7.41421 EndY=7.41421 EndZ=0
    g39: LineSegment StartX=7.41421 StartY=7.41421 StartZ=0 EndX=7.41421 EndY=-7.41421 EndZ=0
    g40: LineSegment StartX=7.41421 StartY=-7.41421 StartZ=0 EndX=-7.41421 EndY=-7.41421 EndZ=0
    g41: LineSegment StartX=-7.41421 StartY=-7.41421 StartZ=0 EndX=-7.41421 EndY=7.41421 EndZ=0
    g42: LineSegment StartX=-10 StartY=10 StartZ=0 EndX=10 EndY=10 EndZ=0
    g43: LineSegment StartX=10 StartY=10 StartZ=0 EndX=10 EndY=-10 EndZ=0
    g44: LineSegment StartX=10 StartY=-10 StartZ=0 EndX=-10 EndY=-10 EndZ=0
    g45: LineSegment StartX=-10 StartY=-10 StartZ=0 EndX=-10 EndY=10 EndZ=0
    g46: LineSegment StartX=4 StartY=4 StartZ=0 EndX=-4 EndY=4 EndZ=0
    g47: LineSegment StartX=-4 StartY=4 StartZ=0 EndX=-4 EndY=-4 EndZ=0
    g48: LineSegment StartX=-4 StartY=-4 StartZ=0 EndX=4 EndY=-4 EndZ=0
    g49: LineSegment StartX=4 StartY=-4 StartZ=0 EndX=4 EndY=4 EndZ=0
    g50: LineSegment StartX=-10 StartY=-10 StartZ=0 EndX=10 EndY=10 EndZ=0
    g51: LineSegment StartX=-10 StartY=10 StartZ=0 EndX=10 EndY=-10 EndZ=0
    g52: LineSegment StartX=2.58579 StartY=4 StartZ=0 EndX=4 EndY=2.58579 EndZ=0
    g53: LineSegment StartX=2.58579 StartY=-4 StartZ=0 EndX=4 EndY=-2.58579 EndZ=0
    g54: LineSegment StartX=-4 StartY=-2.58579 StartZ=0 EndX=-2.58579 EndY=-4 EndZ=0
    g55: LineSegment StartX=10 StartY=3 StartZ=0 EndX=3 EndY=10 EndZ=0
    g56: LineSegment StartX=-3 StartY=10 StartZ=0 EndX=-10 EndY=3 EndZ=0
    g57: LineSegment StartX=-10 StartY=-3 StartZ=0 EndX=-3 EndY=-10 EndZ=0
    g58: LineSegment StartX=3 StartY=-10 StartZ=0 EndX=10 EndY=-3 EndZ=0
    g59: ArcOfCircle CenterX=-9 CenterY=9 CenterZ=0 NormalX=0 NormalY=0 NormalZ=1 AngleXU=0 Radius=1 StartAngle=1.57078 EndAngle=3.14161
    g60: ArcOfCircle CenterX=9 CenterY=9 CenterZ=0 NormalX=0 NormalY=0 NormalZ=1 AngleXU=0 Radius=1 StartAngle=6.28316 EndAngle=7.854
    g61: ArcOfCircle CenterX=9 CenterY=-9 CenterZ=0 NormalX=0 NormalY=0 NormalZ=1 AngleXU=0 Radius=1 StartAngle=4.71238 EndAngle=6.28319
    g62: ArcOfCircle CenterX=-9 CenterY=-9 CenterZ=0 NormalX=0 NormalY=0 NormalZ=1 AngleXU=0 Radius=1 StartAngle=3.14159 EndAngle=4.71241
    g63: LineSegment StartX=-10 StartY=-9 StartZ=0 EndX=10 EndY=-9 EndZ=0
    g64: LineSegment StartX=-10 StartY=8.99998 StartZ=0 EndX=10 EndY=8.99998 EndZ=0
    g65: LineSegment StartX=-8.99998 StartY=10 StartZ=0 EndX=-8.99998 EndY=-10 EndZ=0
    g66: LineSegment StartX=8.99999 StartY=10 StartZ=0 EndX=8.99999 EndY=-10 EndZ=0
    g67: LineSegment StartX=-10 StartY=8.99998 StartZ=0 EndX=-10 EndY=3 EndZ=0
    g68: LineSegment StartX=-10 StartY=-3 StartZ=0 EndX=-10 EndY=-9 EndZ=0
    g69: LineSegment StartX=-8.99998 StartY=10 StartZ=0 EndX=-3 EndY=10 EndZ=0
    g70: LineSegment StartX=8.99999 StartY=10 StartZ=0 EndX=3 EndY=10 EndZ=0
    g71: LineSegment StartX=10 StartY=8.99998 StartZ=0 EndX=10 EndY=3 EndZ=0
    g72: LineSegment StartX=10 StartY=-9 StartZ=0 EndX=10 EndY=-3 EndZ=0
    g73: LineSegment StartX=8.99999 StartY=-10 StartZ=0 EndX=3 EndY=-10 EndZ=0
    g74: LineSegment StartX=-8.99998 StartY=-10 StartZ=0 EndX=-3 EndY=-10 EndZ=0
  constraints (212):
    c: Diameter(g5) = 4.2
    c: Coincident(g42,g43)
    c: Coincident(g43,g44)
    c: Coincident(g44,g45)
    c: Coincident(g45,g42)
    c: Horizontal(g44)
    c: Vertical(g45)
    c: Symmetric(g42,g43,g-1)
    c: Symmetric(g42,g42,g-2)
    c: Coincident(g5,g-1)
    c: Coincident(g38,g41)
    c: Coincident(g7,g29)
    c: Coincident(g29,g30)
    c: Coincident(g27,g28)
    c: Coincident(g3,g28)
    c: Coincident(g3,g4)
    c: Coincident(g6,g7)
    c: Coincident(g2,g27)
    c: Coincident(g2,g37)
    c: Coincident(g8,g30)
    c: Coincident(g8,g37)
    c: Coincident(g8,g31)
    c: Coincident(g13,g33)
    c: Coincident(g9,g10)
    c: Coincident(g11,g12)
    c: Coincident(g12,g34)
    c: Coincident(g33,g34)
    c: Coincident(g40,g41)
    c: Coincident(g31,g32)
    c: Coincident(g9,g32)
    c: Coincident(g14,g36)
    c: Coincident(g17,g18)
    c: Coincident(g39,g40)
    c: Coincident(g18,g19)
    c: Coincident(g35,g36)
    c: Coincident(g13,g35)
    c: Coincident(g19,g20)
    c: Coincident(g16,g17)
    c: Coincident(g0,g1)
    c: Coincident(g1,g25)
    c: Coincident(g22,g23)
    c: Coincident(g23,g24)
    c: Coincident(g21,g22)
    c: Coincident(g38,g39)
    c: Coincident(g25,g26)
    c: Coincident(g2,g26)
    c: Coincident(g20,g21)
    c: Horizontal(g1)
    c: Horizontal(g3)
    c: Horizontal(g12)
    c: Horizontal(g14)
    c: Vertical(g34)
    c: Vertical(g11)
    c: Vertical(g15)
    c: Vertical(g36)
    c: Vertical(g4)
    c: Vertical(g0)
    c: Vertical(g28)
    c: Vertical(g25)
    c: Vertical(g7)
    c: Vertical(g9)
    c: Vertical(g23)
    c: Vertical(g17)
    c: Horizontal(g29)
    c: Horizontal(g6)
    c: Horizontal(g10)
    c: Horizontal(g32)
    c: Horizontal(g22)
    c: Horizontal(g24)
    c: Horizontal(g16)
    c: Horizontal(g18)
    c: Parallel(g30,g27)
    c: Parallel(g27,g35)
    c: Parallel(g35,g19)
    c: Parallel(g21,g26)
    c: Parallel(g31,g33)
    c: Coincident(g46,g47)
    c: Coincident(g47,g48)
    c: Coincident(g48,g49)
    c: Coincident(g49,g46)
    c: Horizontal(g46)
    c: Horizontal(g48)
    c: Vertical(g47)
    c: Vertical(g49)
    c: Horizontal(g2)
    c: Horizontal(g13)
    c: Vertical(g8)
    c: Vertical(g20)
    c: PointOnObject(g2,g46)
    c: PointOnObject(g19,g49)
    c: PointOnObject(g13,g48)
    c: PointOnObject(g8,g47)
    c: Coincident(g50,g44)
    c: Coincident(g50,g42)
    c: Coincident(g51,g42)
    c: Coincident(g51,g43)
    c: PointOnObject(g39,g51)
    c: PointOnObject(g38,g50)
    c: PointOnObject(g38,g51)
    c: Vertical(g39)
    c: Vertical(g41)
    c: Horizontal(g38)
    c: Horizontal(g40)
    c: PointOnObject(g46,g50)
    c: PointOnObject(g46,g51)
    c: PointOnObject(g48,g51)
    c: Parallel(g27,g51)
    c: Parallel(g26,g50)
    c: Perpendicular(g51,g37)
    c: Parallel(g31,g26)
    c: PointOnObject(g4,g42)
    c: PointOnObject(g24,g43)
    c: PointOnObject(g6,g45)
    c: PointOnObject(g10,g45)
    c: PointOnObject(g29,g41)
    c: PointOnObject(g31,g41)
    c: PointOnObject(g33,g40)
    c: PointOnObject(g35,g40)
    c: PointOnObject(g18,g39)
    c: PointOnObject(g21,g39)
    c: PointOnObject(g25,g38)
    c: PointOnObject(g27,g38)
    c: Coincident(g52,g2)
    c: Coincident(g52,g20)
    c: Coincident(g53,g13)
    c: Coincident(g53,g19)
    c: Coincident(g54,g8)
    c: Coincident(g54,g13)
    c: Perpendicular(g50,g54)
    c: Perpendicular(g51,g53)
    c: Perpendicular(g50,g52)
    c: Equal(g37,g52)
    c: Equal(g52,g53)
    c: Equal(g53,g54)
    c: Distance(g37) = 2
    c: Coincident(g14,g15)
    c: PointOnObject(g6,g24)
    c: PointOnObject(g9,g16)
    c: PointOnObject(g11,g4)
    c: PointOnObject(g14,g0)
    c: PointOnObject(g11,g44)
    c: PointOnObject(g15,g44)
    c: DistanceX(g42) = 10
    c: DistanceY(g49,g49) = 8
    c: DistanceY(g18,g21) = 12
    c: Coincident(g56,g4)
    c: Coincident(g57,g10)
    c: Coincident(g58,g15)
    c: Perpendicular(g51,g58)
    c: Perpendicular(g50,g55)
    c: Perpendicular(g51,g56)
    c: Equal(g58,g57)
    c: Equal(g57,g55)
    c: DistanceY(g16,g24) = 6
    c: Equal(g42,g43)
    c: Coincident(g55,g0)
    c: Coincident(g55,g24)
    c: Coincident(g56,g6)
    c: Coincident(g11,g57)
    c: Coincident(g16,g58)
    c: DistanceX(g6,g6) = 2
    c: Equal(g6,g10)
    c: Equal(g10,g24)
    c: Equal(g24,g16)
    c: Equal(g16,g15)
    c: Equal(g15,g11)
    c: Equal(g11,g4)
    c: Equal(g4,g0)
    c: PointOnObject(g59,g51)
    c: PointOnObject(g59,g45)
    c: PointOnObject(g59,g42)
    c: PointOnObject(g60,g42)
    c: PointOnObject(g60,g43)
    c: PointOnObject(g61,g51)
    c: PointOnObject(g61,g43)
    c: PointOnObject(g61,g44)
    c: PointOnObject(g62,g50)
    c: PointOnObject(g62,g44)
    c: PointOnObject(g62,g45)
    c: Radius(g62) = 1
    c: Equal(g62,g59)
    c: Equal(g59,g60)
    c: Equal(g60,g61)
    c: Coincident(g63,g62)
    c: Coincident(g63,g61)
    c: Horizontal(g63)
    c: Coincident(g64,g59)
    c: Coincident(g64,g60)
    c: Horizontal(g64)
    c: Coincident(g65,g59)
    c: Coincident(g65,g62)
    c: Vertical(g65)
    c: Coincident(g66,g60)
    c: Coincident(g66,g61)
    c: Vertical(g66)
    c: PointOnObject(g62,g63)
    c: Coincident(g67,g59)
    c: Coincident(g67,g6)
    c: Coincident(g68,g10)
    c: Coincident(g68,g62)
    c: Coincident(g69,g59)
    c: Coincident(g69,g4)
    c: Coincident(g70,g60)
    c: Coincident(g70,g0)
    c: Coincident(g71,g60)
    c: Coincident(g71,g24)
    c: Coincident(g72,g61)
    c: Coincident(g72,g16)
    c: Coincident(g73,g61)
    c: Coincident(g73,g15)
    c: Coincident(g74,g62)
    c: Coincident(g74,g11)
FEATURE [PartDesign::Pad] Pad023  label="Frame_P_Pad"
  Direction = (0,-1,-2e-16)
  Length = 246
  Length2 = 100
  Midplane = true
  Placement = pos=(0,0,0) rot=(1,0,0;1.5708rad)
  Profile = -> Sketch044
  Type = 0
  expr: Length = <<Common>>#<<Parameters>>.boxsize_y
FEATURE [Sketcher::SketchObject] Sketch054  label="Frame_P_SideHoles_Sketch"
  ExternalGeometry = -> [Pad023]
  FullyConstrained = true
  MapMode = 5
  Placement = pos=(0,0,0) rot=(0.57735,0.57735,0.57735;2.0944rad)
  Support = -> [YZ_Plane035]
  expr: Constraints[1] = -<<Common>>#<<Parameters>>.cpointpos
  sketch-geometry (3):
    g0: Circle CenterX=-64 CenterY=0 CenterZ=0 NormalX=0 NormalY=0 NormalZ=1 AngleXU=0 Radius=2.5
    g1: Circle CenterX=-113 CenterY=0 CenterZ=0 NormalX=0 NormalY=0 NormalZ=1 AngleXU=0 Radius=2.5
    g2: Circle CenterX=113 CenterY=0 CenterZ=0 NormalX=0 NormalY=0 NormalZ=1 AngleXU=0 Radius=2.5
  constraints (9):
    c: PointOnObject(g0,g-1)
    c: DistanceX(g0) = -64
    c: Diameter(g0) = 5
    c: PointOnObject(g1,g-1)
    c: PointOnObject(g2,g-1)
    c: Equal(g2,g1)
    c: Equal(g1,g0)
    c: DistanceX(g-3,g1) = 10
    c: DistanceX(g2,g-4) = 10
FEATURE [PartDesign::Pocket] Pocket010  label="Frame_P_SideHoles"
  BaseFeature = -> Pad023
  Direction = (-1,2e-16,-3e-16)
  Length = 5
  Length2 = 100
  Midplane = true
  Placement = pos=(0,0,0) rot=(1,0,0;1.5708rad)
  Profile = -> Sketch054
  Type = 1
FEATURE [Sketcher::SketchObject] Sketch094  label="Frame_P_TopHoles_Sketch"
  FullyConstrained = true
  MapMode = 5
  Placement = pos=(0,-9e-16,4) rot=(0,0,1;3.14159rad)
  Support = -> [Pad023]
  expr: Constraints[4] = <<Common>>#<<Parameters>>.bolt_y
  sketch-geometry (2):
    g0: Circle CenterX=0 CenterY=113 CenterZ=0 NormalX=0 NormalY=0 NormalZ=1 AngleXU=0 Radius=2.75
    g1: Circle CenterX=0 CenterY=-113 CenterZ=0 NormalX=0 NormalY=0 NormalZ=1 AngleXU=0 Radius=2.75
  constraints (5):
    c: PointOnObject(g0,g-2)
    c: Diameter(g1) = 5.5
    c: Equal(g1,g0)
    c: Symmetric(g0,g1,g-1)
    c: DistanceY(g0) = 113
FEATURE [PartDesign::Pocket] Pocket037  label="Frame_P_TopHoles"
  BaseFeature = -> Pocket010
  Direction = (0,2e-16,-1)
  Length = 5
  Length2 = 100
  Midplane = true
  Placement = pos=(0,0,0) rot=(1,0,0;1.5708rad)
  Profile = -> Sketch094
  Type = 1
FEATURE [PartDesign::CoordinateSystem] Local_CS310  label="LCS_Frame_PS_A"
  AttacherType = Attacher::AttachEngine3D
  AttachmentOffset = pos=(0,92,0) rot=(0,0,1;0rad)
  MapMode = 5
  Placement = pos=(0,92,0) rot=(0,0,1;0rad)
  Support = -> [XY_Plane035]
  expr: .AttachmentOffset.Base.y = <<Common>>#<<Parameters>>.collpos_y
FEATURE [PartDesign::CoordinateSystem] Local_CS311  label="LCS_Frame_PS_F"
  AttacherType = Attacher::AttachEngine3D
  AttachmentOffset = pos=(0,-64,0) rot=(0,0,1;0rad)
  MapMode = 5
  Placement = pos=(0,-64,0) rot=(0,0,1;0rad)
  Support = -> [XY_Plane035]
  expr: .AttachmentOffset.Base.y = -<<Common>>#<<Parameters>>.cpointpos
FEATURE [PartDesign::CoordinateSystem] Local_CS  label="LCS_RockerPoint_F"
  AttacherType = Attacher::AttachEngine3D
  MapMode = 45
  Placement = pos=(-1.14085e-10,-113,3.94e-14) rot=(0.57735,0.57735,0.57735;4.18879rad)
  Support = -> [Pocket037]
FEATURE [PartDesign::CoordinateSystem] Local_CS312  label="LCS_RockerPoint_A"
  AttacherType = Attacher::AttachEngine3D
  MapMode = 45
  Placement = pos=(-1.14085e-10,113,-1.09e-14) rot=(0.57735,0.57735,0.57735;4.18879rad)
  Support = -> [Pocket037]
FEATURE [PartDesign::CoordinateSystem] Local_CS318  label="LCS_PoleBase_A"
  AttacherType = Attacher::AttachEngine3D
  AttachmentOffset = pos=(0,113,10) rot=(0,0,1;0rad)
  MapMode = 5
  Placement = pos=(0,113,10) rot=(0,0,1;0rad)
  Support = -> [XY_Plane035]
  expr: .AttachmentOffset.Base.y = <<Common>>#<<Parameters>>.bolt_y
FEATURE [PartDesign::CoordinateSystem] Local_CS319  label="LCS_PoleBase_F"
  AttacherType = Attacher::AttachEngine3D
  AttachmentOffset = pos=(0,-113,10) rot=(0,0,1;0rad)
  MapMode = 5
  Placement = pos=(0,-113,10) rot=(0,0,1;0rad)
  Support = -> [XY_Plane035]
  expr: .AttachmentOffset.Base.y = -<<Common>>#<<Parameters>>.bolt_y
FEATURE [PartDesign::Body] Body024  label="Frame_PS"
  Group = -> [Sketch044,Pad023,Sketch054,Pocket010,Sketch094,Pocket037,Local_CS310,Local_CS311,Local_CS,Local_CS312,Local_CS318,Local_CS319]
  Origin = -> Origin035
  Placement = pos=(113,0,-62) rot=(0,0,1;0rad)
  Tip = -> Pocket037
  expr: .Placement.Base.x = <<Common>>#<<Parameters>>.bolt_x
  expr: .Placement.Base.z = <<Common>>#<<Parameters>>.datum_uppercell - <<Common>>#<<Parameters>>.pri_cellfloat - 10
COMPONENT P5 — recipe-attached ("Frame_A", modeled in this document).
Construction recipe (the document's own serialized feature program — sketch geometry with constraints, then the solid features built on it; lengths are millimeters unless a unit is written):

FEATURE [Sketcher::SketchObject] Sketch045  label="Frame_A_Sketch"
  FullyConstrained = true
  MapMode = 5
  Placement = pos=(0,0,0) rot=(0.57735,0.57735,0.57735;2.0944rad)
  Support = -> [YZ_Plane036]
  sketch-geometry (75):
    g0: LineSegment StartX=3 StartY=10 StartZ=0 EndX=3 EndY=8 EndZ=0
    g1: LineSegment StartX=3 StartY=8 StartZ=0 EndX=6 EndY=8 EndZ=0
    g2: LineSegment StartX=2.58579 StartY=4 StartZ=0 EndX=-2.58579 EndY=4 EndZ=0
    g3: LineSegment StartX=-6 StartY=8 StartZ=0 EndX=-3 EndY=8 EndZ=0
    g4: LineSegment StartX=-3 StartY=8 StartZ=0 EndX=-3 EndY=10 EndZ=0
    g5: Circle CenterX=0 CenterY=0 CenterZ=0 NormalX=0 NormalY=0 NormalZ=1 AngleXU=0 Radius=2.1
    g6: LineSegment StartX=-10 StartY=3 StartZ=0 EndX=-8 EndY=3 EndZ=0
    g7: LineSegment StartX=-8 StartY=3 StartZ=0 EndX=-8 EndY=6 EndZ=0
    g8: LineSegment StartX=-4 StartY=2.58579 StartZ=0 EndX=-4 EndY=-2.58579 EndZ=0
    g9: LineSegment StartX=-8 StartY=-6 StartZ=0 EndX=-8 EndY=-3 EndZ=0
    g10: LineSegment StartX=-8 StartY=-3 StartZ=0 EndX=-10 EndY=-3 EndZ=0
    g11: LineSegment StartX=-3 StartY=-10 StartZ=0 EndX=-3 EndY=-8 EndZ=0
    g12: LineSegment StartX=-3 StartY=-8 StartZ=0 EndX=-6 EndY=-8 EndZ=0
    g13: LineSegment StartX=-2.58579 StartY=-4 StartZ=0 EndX=2.58579 EndY=-4 EndZ=0
    g14: LineSegment StartX=6 StartY=-8 StartZ=0 EndX=3 EndY=-8 EndZ=0
    g15: LineSegment StartX=3 StartY=-8 StartZ=0 EndX=3 EndY=-10 EndZ=0
    g16: LineSegment StartX=10 StartY=-3 StartZ=0 EndX=8 EndY=-3 EndZ=0
    g17: LineSegment StartX=8 StartY=-3 StartZ=0 EndX=8 EndY=-6 EndZ=0
    g18: LineSegment StartX=8 StartY=-6 StartZ=0 EndX=7.41421 EndY=-6 EndZ=0
    g19: LineSegment StartX=7.41421 StartY=-6 StartZ=0 EndX=4 EndY=-2.58579 EndZ=0
    g20: LineSegment StartX=4 StartY=-2.58579 StartZ=0 EndX=4 EndY=2.58579 EndZ=0
    g21: LineSegment StartX=4 StartY=2.58579 StartZ=0 EndX=7.41421 EndY=6 EndZ=0
    g22: LineSegment StartX=7.41421 StartY=6 StartZ=0 EndX=8 EndY=6 EndZ=0
    g23: LineSegment StartX=8 StartY=6 StartZ=0 EndX=8 EndY=3 EndZ=0
    g24: LineSegment StartX=8 StartY=3 StartZ=0 EndX=10 EndY=3 EndZ=0
    g25: LineSegment StartX=6 StartY=8 StartZ=0 EndX=6 EndY=7.41421 EndZ=0
    g26: LineSegment StartX=6 StartY=7.41421 StartZ=0 EndX=2.58579 EndY=4 EndZ=0
    g27: LineSegment StartX=-2.58579 StartY=4 StartZ=0 EndX=-6 EndY=7.41421 EndZ=0
    g28: LineSegment StartX=-6 StartY=7.41421 StartZ=0 EndX=-6 EndY=8 EndZ=0
    g29: LineSegment StartX=-8 StartY=6 StartZ=0 EndX=-7.41421 EndY=6 EndZ=0
    g30: LineSegment StartX=-7.41421 StartY=6 StartZ=0 EndX=-4 EndY=2.58579 EndZ=0
    g31: LineSegment StartX=-4 StartY=-2.58579 StartZ=0 EndX=-7.41421 EndY=-6 EndZ=0
    g32: LineSegment StartX=-7.41421 StartY=-6 StartZ=0 EndX=-8 EndY=-6 EndZ=0
    g33: LineSegment StartX=-2.58579 StartY=-4 StartZ=0 EndX=-6 EndY=-7.41421 EndZ=0
    g34: LineSegment StartX=-6 StartY=-7.41421 StartZ=0 EndX=-6 EndY=-8 EndZ=0
    g35: LineSegment StartX=2.58579 StartY=-4 StartZ=0 EndX=6 EndY=-7.41421 EndZ=0
    g36: LineSegment StartX=6 StartY=-7.41421 StartZ=0 EndX=6 EndY=-8 EndZ=0
    g37: LineSegment StartX=-4 StartY=2.58579 StartZ=0 EndX=-2.58579 EndY=4 EndZ=0
    g38: LineSegment StartX=-7.41421 StartY=7.41421 StartZ=0 EndX=7.41421 EndY=7.41421 EndZ=0
    g39: LineSegment StartX=7.41421 StartY=7.41421 StartZ=0 EndX=7.41421 EndY=-7.41421 EndZ=0
    g40: LineSegment StartX=7.41421 StartY=-7.41421 StartZ=0 EndX=-7.41421 EndY=-7.41421 EndZ=0
    g41: LineSegment StartX=-7.41421 StartY=-7.41421 StartZ=0 EndX=-7.41421 EndY=7.41421 EndZ=0
    g42: LineSegment StartX=-10 StartY=10 StartZ=0 EndX=10 EndY=10 EndZ=0
    g43: LineSegment StartX=10 StartY=10 StartZ=0 EndX=10 EndY=-10 EndZ=0
    g44: LineSegment StartX=10 StartY=-10 StartZ=0 EndX=-10 EndY=-10 EndZ=0
    g45: LineSegment StartX=-10 StartY=-10 StartZ=0 EndX=-10 EndY=10 EndZ=0
    g46: LineSegment StartX=4 StartY=4 StartZ=0 EndX=-4 EndY=4 EndZ=0
    g47: LineSegment StartX=-4 StartY=4 StartZ=0 EndX=-4 EndY=-4 EndZ=0
    g48: LineSegment StartX=-4 StartY=-4 StartZ=0 EndX=4 EndY=-4 EndZ=0
    g49: LineSegment StartX=4 StartY=-4 StartZ=0 EndX=4 EndY=4 EndZ=0
    g50: LineSegment StartX=-10 StartY=-10 StartZ=0 EndX=10 EndY=10 EndZ=0
    g51: LineSegment StartX=-10 StartY=10 StartZ=0 EndX=10 EndY=-10 EndZ=0
    g52: LineSegment StartX=2.58579 StartY=4 StartZ=0 EndX=4 EndY=2.58579 EndZ=0
    g53: LineSegment StartX=2.58579 StartY=-4 StartZ=0 EndX=4 EndY=-2.58579 EndZ=0
    g54: LineSegment StartX=-4 StartY=-2.58579 StartZ=0 EndX=-2.58579 EndY=-4 EndZ=0
    g55: LineSegment StartX=10 StartY=3 StartZ=0 EndX=3 EndY=10 EndZ=0
    g56: LineSegment StartX=-3 StartY=10 StartZ=0 EndX=-10 EndY=3 EndZ=0
    g57: LineSegment StartX=-10 StartY=-3 StartZ=0 EndX=-3 EndY=-10 EndZ=0
    g58: LineSegment StartX=3 StartY=-10 StartZ=0 EndX=10 EndY=-3 EndZ=0
    g59: ArcOfCircle CenterX=-9 CenterY=9 CenterZ=0 NormalX=0 NormalY=0 NormalZ=1 AngleXU=0 Radius=1 StartAngle=1.57078 EndAngle=3.14161
    g60: ArcOfCircle CenterX=9 CenterY=9 CenterZ=0 NormalX=0 NormalY=0 NormalZ=1 AngleXU=0 Radius=1 StartAngle=6.28316 EndAngle=7.854
    g61: ArcOfCircle CenterX=9 CenterY=-9 CenterZ=0 NormalX=0 NormalY=0 NormalZ=1 AngleXU=0 Radius=1 StartAngle=4.71238 EndAngle=6.28319
    g62: ArcOfCircle CenterX=-9 CenterY=-9 CenterZ=0 NormalX=0 NormalY=0 NormalZ=1 AngleXU=0 Radius=1 StartAngle=3.14159 EndAngle=4.71241
    g63: LineSegment StartX=-10 StartY=-9 StartZ=0 EndX=10 EndY=-9 EndZ=0
    g64: LineSegment StartX=-10 StartY=8.99998 StartZ=0 EndX=10 EndY=8.99998 EndZ=0
    g65: LineSegment StartX=-8.99998 StartY=10 StartZ=0 EndX=-8.99998 EndY=-10 EndZ=0
    g66: LineSegment StartX=8.99999 StartY=10 StartZ=0 EndX=8.99999 EndY=-10 EndZ=0
    g67: LineSegment StartX=-10 StartY=8.99998 StartZ=0 EndX=-10 EndY=3 EndZ=0
    g68: LineSegment StartX=-10 StartY=-3 StartZ=0 EndX=-10 EndY=-9 EndZ=0
    g69: LineSegment StartX=-8.99998 StartY=10 StartZ=0 EndX=-3 EndY=10 EndZ=0
    g70: LineSegment StartX=8.99999 StartY=10 StartZ=0 EndX=3 EndY=10 EndZ=0
    g71: LineSegment StartX=10 StartY=8.99998 StartZ=0 EndX=10 EndY=3 EndZ=0
    g72: LineSegment StartX=10 StartY=-9 StartZ=0 EndX=10 EndY=-3 EndZ=0
    g73: LineSegment StartX=8.99999 StartY=-10 StartZ=0 EndX=3 EndY=-10 EndZ=0
    g74: LineSegment StartX=-8.99998 StartY=-10 StartZ=0 EndX=-3 EndY=-10 EndZ=0
  constraints (212):
    c: Diameter(g5) = 4.2
    c: Coincident(g42,g43)
    c: Coincident(g43,g44)
    c: Coincident(g44,g45)
    c: Coincident(g45,g42)
    c: Horizontal(g44)
    c: Vertical(g45)
    c: Symmetric(g42,g43,g-1)
    c: Symmetric(g42,g42,g-2)
    c: Coincident(g5,g-1)
    c: Coincident(g38,g41)
    c: Coincident(g7,g29)
    c: Coincident(g29,g30)
    c: Coincident(g27,g28)
    c: Coincident(g3,g28)
    c: Coincident(g3,g4)
    c: Coincident(g6,g7)
    c: Coincident(g2,g27)
    c: Coincident(g2,g37)
    c: Coincident(g8,g30)
    c: Coincident(g8,g37)
    c: Coincident(g8,g31)
    c: Coincident(g13,g33)
    c: Coincident(g9,g10)
    c: Coincident(g11,g12)
    c: Coincident(g12,g34)
    c: Coincident(g33,g34)
    c: Coincident(g40,g41)
    c: Coincident(g31,g32)
    c: Coincident(g9,g32)
    c: Coincident(g14,g36)
    c: Coincident(g17,g18)
    c: Coincident(g39,g40)
    c: Coincident(g18,g19)
    c: Coincident(g35,g36)
    c: Coincident(g13,g35)
    c: Coincident(g19,g20)
    c: Coincident(g16,g17)
    c: Coincident(g0,g1)
    c: Coincident(g1,g25)
    c: Coincident(g22,g23)
    c: Coincident(g23,g24)
    c: Coincident(g21,g22)
    c: Coincident(g38,g39)
    c: Coincident(g25,g26)
    c: Coincident(g2,g26)
    c: Coincident(g20,g21)
    c: Horizontal(g1)
    c: Horizontal(g3)
    c: Horizontal(g12)
    c: Horizontal(g14)
    c: Vertical(g34)
    c: Vertical(g11)
    c: Vertical(g15)
    c: Vertical(g36)
    c: Vertical(g4)
    c: Vertical(g0)
    c: Vertical(g28)
    c: Vertical(g25)
    c: Vertical(g7)
    c: Vertical(g9)
    c: Vertical(g23)
    c: Vertical(g17)
    c: Horizontal(g29)
    c: Horizontal(g6)
    c: Horizontal(g10)
    c: Horizontal(g32)
    c: Horizontal(g22)
    c: Horizontal(g24)
    c: Horizontal(g16)
    c: Horizontal(g18)
    c: Parallel(g30,g27)
    c: Parallel(g27,g35)
    c: Parallel(g35,g19)
    c: Parallel(g21,g26)
    c: Parallel(g31,g33)
    c: Coincident(g46,g47)
    c: Coincident(g47,g48)
    c: Coincident(g48,g49)
    c: Coincident(g49,g46)
    c: Horizontal(g46)
    c: Horizontal(g48)
    c: Vertical(g47)
    c: Vertical(g49)
    c: Horizontal(g2)
    c: Horizontal(g13)
    c: Vertical(g8)
    c: Vertical(g20)
    c: PointOnObject(g2,g46)
    c: PointOnObject(g19,g49)
    c: PointOnObject(g13,g48)
    c: PointOnObject(g8,g47)
    c: Coincident(g50,g44)
    c: Coincident(g50,g42)
    c: Coincident(g51,g42)
    c: Coincident(g51,g43)
    c: PointOnObject(g39,g51)
    c: PointOnObject(g38,g50)
    c: PointOnObject(g38,g51)
    c: Vertical(g39)
    c: Vertical(g41)
    c: Horizontal(g38)
    c: Horizontal(g40)
    c: PointOnObject(g46,g50)
    c: PointOnObject(g46,g51)
    c: PointOnObject(g48,g51)
    c: Parallel(g27,g51)
    c: Parallel(g26,g50)
    c: Perpendicular(g51,g37)
    c: Parallel(g31,g26)
    c: PointOnObject(g4,g42)
    c: PointOnObject(g24,g43)
    c: PointOnObject(g6,g45)
    c: PointOnObject(g10,g45)
    c: PointOnObject(g29,g41)
    c: PointOnObject(g31,g41)
    c: PointOnObject(g33,g40)
    c: PointOnObject(g35,g40)
    c: PointOnObject(g18,g39)
    c: PointOnObject(g21,g39)
    c: PointOnObject(g25,g38)
    c: PointOnObject(g27,g38)
    c: Coincident(g52,g2)
    c: Coincident(g52,g20)
    c: Coincident(g53,g13)
    c: Coincident(g53,g19)
    c: Coincident(g54,g8)
    c: Coincident(g54,g13)
    c: Perpendicular(g50,g54)
    c: Perpendicular(g51,g53)
    c: Perpendicular(g50,g52)
    c: Equal(g37,g52)
    c: Equal(g52,g53)
    c: Equal(g53,g54)
    c: Distance(g37) = 2
    c: Coincident(g14,g15)
    c: PointOnObject(g6,g24)
    c: PointOnObject(g9,g16)
    c: PointOnObject(g11,g4)
    c: PointOnObject(g14,g0)
    c: PointOnObject(g11,g44)
    c: PointOnObject(g15,g44)
    c: DistanceX(g42) = 10
    c: DistanceY(g49,g49) = 8
    c: DistanceY(g18,g21) = 12
    c: Coincident(g56,g4)
    c: Coincident(g57,g10)
    c: Coincident(g58,g15)
    c: Perpendicular(g51,g58)
    c: Perpendicular(g50,g55)
    c: Perpendicular(g51,g56)
    c: Equal(g58,g57)
    c: Equal(g57,g55)
    c: DistanceY(g16,g24) = 6
    c: Equal(g42,g43)
    c: Coincident(g55,g0)
    c: Coincident(g55,g24)
    c: Coincident(g56,g6)
    c: Coincident(g11,g57)
    c: Coincident(g16,g58)
    c: DistanceX(g6,g6) = 2
    c: Equal(g6,g10)
    c: Equal(g10,g24)
    c: Equal(g24,g16)
    c: Equal(g16,g15)
    c: Equal(g15,g11)
    c: Equal(g11,g4)
    c: Equal(g4,g0)
    c: PointOnObject(g59,g51)
    c: PointOnObject(g59,g45)
    c: PointOnObject(g59,g42)
    c: PointOnObject(g60,g42)
    c: PointOnObject(g60,g43)
    c: PointOnObject(g61,g51)
    c: PointOnObject(g61,g43)
    c: PointOnObject(g61,g44)
    c: PointOnObject(g62,g50)
    c: PointOnObject(g62,g44)
    c: PointOnObject(g62,g45)
    c: Radius(g62) = 1
    c: Equal(g62,g59)
    c: Equal(g59,g60)
    c: Equal(g60,g61)
    c: Coincident(g63,g62)
    c: Coincident(g63,g61)
    c: Horizontal(g63)
    c: Coincident(g64,g59)
    c: Coincident(g64,g60)
    c: Horizontal(g64)
    c: Coincident(g65,g59)
    c: Coincident(g65,g62)
    c: Vertical(g65)
    c: Coincident(g66,g60)
    c: Coincident(g66,g61)
    c: Vertical(g66)
    c: PointOnObject(g62,g63)
    c: Coincident(g67,g59)
    c: Coincident(g67,g6)
    c: Coincident(g68,g10)
    c: Coincident(g68,g62)
    c: Coincident(g69,g59)
    c: Coincident(g69,g4)
    c: Coincident(g70,g60)
    c: Coincident(g70,g0)
    c: Coincident(g71,g60)
    c: Coincident(g71,g24)
    c: Coincident(g72,g61)
    c: Coincident(g72,g16)
    c: Coincident(g73,g61)
    c: Coincident(g73,g15)
    c: Coincident(g74,g62)
    c: Coincident(g74,g11)
FEATURE [PartDesign::Pad] Pad024  label="Frame_A_Pad"
  Direction = (1,-2e-16,3e-16)
  Length = 206
  Length2 = 100
  Midplane = true
  Placement = pos=(0,0,0) rot=(0.57735,0.57735,0.57735;2.0944rad)
  Profile = -> Sketch045
  Type = 0
  expr: Length = <<Common>>#<<Parameters>>.bolt_x * 2 - 20
FEATURE [PartDesign::Plane] DatumPlane009  label="DatumPlane_Frame_A_Top"
  AttachmentOffset = pos=(0,0,10) rot=(0,0,1;1.5708rad)
  Length = 70.2978
  MapMode = 5
  Placement = pos=(0,0,10) rot=(0,0,1;1.5708rad)
  ResizeMode = 0
  Support = -> [XY_Plane036]
  Width = 226.298
FEATURE [Sketcher::SketchObject] Sketch046  label="Frame_A_CollHoles_Sketch"
  FullyConstrained = true
  MapMode = 5
  Placement = pos=(0,0,10) rot=(0,0,1;1.5708rad)
  Support = -> [DatumPlane009]
  expr: Constraints[3] = <<Common>>#<<Parameters>>.collpos_y
  expr: Constraints[4] = <<Common>>#<<Parameters>>.collbolt
  sketch-geometry (3):
    g0: Circle CenterX=0 CenterY=0 CenterZ=0 NormalX=0 NormalY=0 NormalZ=1 AngleXU=0 Radius=3
    g1: Circle CenterX=0 CenterY=-92 CenterZ=0 NormalX=0 NormalY=0 NormalZ=1 AngleXU=0 Radius=3
    g2: Circle CenterX=0 CenterY=92 CenterZ=0 NormalX=0 NormalY=0 NormalZ=1 AngleXU=0 Radius=3
  constraints (7):
    c: Coincident(g0,g-1)
    c: PointOnObject(g1,g-2)
    c: Symmetric(g2,g1,g-1)
    c: DistanceY(g2) = 92
    c: Diameter(g0) = 6
    c: Equal(g0,g2)
    c: Equal(g0,g1)
FEATURE [PartDesign::Hole] Hole025  label="Frame_A_CollHoles"
  BaseFeature = -> Pad024
  CustomThreadClearance = 0
  Depth = 25
  DepthType = 1
  Diameter = 6.4
  DrillForDepth = false
  DrillPoint = 1
  DrillPointAngle = 118
  HoleCutCountersinkAngle = 90
  HoleCutCustomValues = false
  HoleCutDepth = 0
  HoleCutDiameter = 6.1
  HoleCutType = 0
  ModelThread = false
  Placement = pos=(0,0,0) rot=(0.57735,0.57735,0.57735;2.0944rad)
  Profile = -> Sketch046
  Tapered = false
  TaperedAngle = 90
  ThreadClass = 5
  ThreadDepth = 23.5
  ThreadDepthType = 0
  ThreadDirection = 0
  ThreadFit = 1
  ThreadSize = 14
  ThreadType = 1
  Threaded = false
  UseCustomThreadClearance = false
FEATURE [PartDesign::CoordinateSystem] Local_CS090  label="LCS_Frame_A_Bolt_P"
  AttacherType = Attacher::AttachEngine3D
  AttachmentOffset = pos=(0,0,-10) rot=(0,0,1;0rad)
  MapMode = 11
  Placement = pos=(113,-4.8e-14,4.4e-14) rot=(0.707107,0,-0.707107;3.14159rad)
  Support = -> [Pad024]
FEATURE [PartDesign::CoordinateSystem] Local_CS091  label="LCS_Frame_A_Bolt_S"
  AttacherType = Attacher::AttachEngine3D
  AttachmentOffset = pos=(0,0,10) rot=(0,0,1;0rad)
  MapMode = 11
  Placement = pos=(-113,4.8e-14,-4.49e-14) rot=(0.707107,0,-0.707107;3.14159rad)
  Support = -> [Pad024]
FEATURE [PartDesign::CoordinateSystem] Local_CS095  label="LCS_LowerCell_Float"
  AttacherType = Attacher::AttachEngine3D
  AttachmentOffset = pos=(0,-92,25) rot=(0,0,1;0rad)
  MapMode = 5
  Placement = pos=(0,-92,25) rot=(0,0,1;0rad)
  Support = -> [XY_Plane036]
  expr: .AttachmentOffset.Base.y = -<<Common>>#<<Parameters>>.collpos_y
  expr: .AttachmentOffset.Base.z = <<Common>>#<<Parameters>>.datum_uppercell - <<Common>>#<<Parameters>>.datum_lowercell
FEATURE [PartDesign::CoordinateSystem] Local_CS096  label="LCS_LowerCell_Pivot"
  AttacherType = Attacher::AttachEngine3D
  AttachmentOffset = pos=(0,-92,145) rot=(0,0,1;0rad)
  MapMode = 5
  Placement = pos=(0,-92,145) rot=(0,0,1;0rad)
  Support = -> [XY_Plane036]
  expr: .AttachmentOffset.Base.y = -<<Common>>#<<Parameters>>.collpos_y
  expr: .AttachmentOffset.Base.z = <<Common>>#<<Parameters>>.datum_rocker_z - <<Common>>#<<Parameters>>.datum_lowercell
FEATURE [PartDesign::CoordinateSystem] Local_CS313  label="LCS_Frame_A_Counterweight"
  AttacherType = Attacher::AttachEngine3D
  MapMode = 45
  Placement = pos=(1.61607e-09,-3.92884e-05,-2.63357e-06) rot=(0.577349,0.577354,0.577349;2.09439rad)
  Support = -> [Hole025]
FEATURE [PartDesign::CoordinateSystem] Local_CS315  label="LCS_Frame_A_Collpos_P"
  AttacherType = Attacher::AttachEngine3D
  AttachmentOffset = pos=(92,0,0) rot=(0,0,1;0rad)
  MapMode = 5
  Placement = pos=(92,0,0) rot=(0,0,1;0rad)
  Support = -> [XY_Plane036]
  expr: .AttachmentOffset.Base.x = <<Common>>#<<Parameters>>.collpos_y
FEATURE [PartDesign::CoordinateSystem] Local_CS316  label="LCS_Frame_A_Collpos_S"
  AttacherType = Attacher::AttachEngine3D
  AttachmentOffset = pos=(-92,0,0) rot=(0,0,1;0rad)
  MapMode = 5
  Placement = pos=(-92,0,0) rot=(0,0,1;0rad)
  Support = -> [XY_Plane036]
  expr: .AttachmentOffset.Base.x = -<<Common>>#<<Parameters>>.collpos_y
FEATURE [PartDesign::Body] Body025  label="Frame_A"
  Group = -> [Sketch045,Pad024,DatumPlane009,Sketch046,Hole025,Local_CS090,Local_CS091,Local_CS095,Local_CS096,Local_CS313,Local_CS315,Local_CS316]
  Origin = -> Origin036
  Placement = pos=(0,92,-62) rot=(0,0,1;0rad)
  Tip = -> Hole025
  expr: .Placement.Base.y = <<Common>>#<<Parameters>>.collpos_y
  expr: .Placement.Base.z = <<Common>>#<<Parameters>>.datum_uppercell - <<Common>>#<<Parameters>>.pri_cellfloat - 10
COMPONENT P6 — recipe-attached ("Frame_F", modeled in this document).
Construction recipe (the document's own serialized feature program — sketch geometry with constraints, then the solid features built on it; lengths are millimeters unless a unit is written):

FEATURE [PartDesign::FeatureBase] Clone008  label="Frame_F_Clone"
  BaseFeature = -> Pad024
  Placement = pos=(0,0,0) rot=(0.57735,0.57735,0.57735;2.0944rad)
FEATURE [PartDesign::Plane] DatumPlane012  label="DatumPlane_Frame_F_Top"
  AttachmentOffset = pos=(0,0,10) rot=(0,0,1;0rad)
  Length = 226.298
  MapMode = 5
  Placement = pos=(0,0,10) rot=(0,0,1;0rad)
  ResizeMode = 0
  Support = -> [XY_Plane051]
  Width = 70.2978
FEATURE [Sketcher::SketchObject] Sketch059  label="Frame_F_CollHoles_Sketch"
  FullyConstrained = true
  MapMode = 5
  Placement = pos=(0,0,10) rot=(0,0,1;0rad)
  Support = -> [DatumPlane012]
  expr: Constraints[1] = <<Common>>#<<Parameters>>.collbolt
  sketch-geometry (1):
    g0: Circle CenterX=0 CenterY=0 CenterZ=0 NormalX=0 NormalY=0 NormalZ=1 AngleXU=0 Radius=3
  constraints (2):
    c: Coincident(g0,g-1)
    c: Diameter(g0) = 6
FEATURE [PartDesign::Hole] Hole029  label="Frame_F_CollHoles"
  BaseFeature = -> Clone008
  CustomThreadClearance = 0
  Depth = 25
  DepthType = 1
  Diameter = 5
  DrillForDepth = false
  DrillPoint = 1
  DrillPointAngle = 118
  HoleCutCountersinkAngle = 90
  HoleCutCustomValues = false
  HoleCutDepth = 0
  HoleCutDiameter = 6.1
  HoleCutType = 0
  ModelThread = false
  Placement = pos=(0,0,0) rot=(0.57735,0.57735,0.57735;2.0944rad)
  Profile = -> Sketch059
  Tapered = false
  TaperedAngle = 90
  ThreadClass = 5
  ThreadDepth = 23.5
  ThreadDepthType = 0
  ThreadDirection = 0
  ThreadFit = 0
  ThreadSize = 14
  ThreadType = 1
  Threaded = true
  UseCustomThreadClearance = false
FEATURE [PartDesign::CoordinateSystem] Local_CS089  label="LCS_Frame_F_Bolt_P"
  AttacherType = Attacher::AttachEngine3D
  AttachmentOffset = pos=(0,0,2) rot=(0,0,1;0rad)
  MapMode = 11
  Placement = pos=(105,-4.64e-14,4.07e-14) rot=(0.707107,0,0.707107;3.14159rad)
  Support = -> [Hole029]
FEATURE [PartDesign::CoordinateSystem] Local_CS092  label="LCS_Frame_F_Bolt_S"
  AttacherType = Attacher::AttachEngine3D
  AttachmentOffset = pos=(0,0,2) rot=(0,0,1;0rad)
  MapMode = 11
  Placement = pos=(-105,4.64e-14,-4.11e-14) rot=(0.707107,0,-0.707107;3.14159rad)
  Support = -> [Hole029]
FEATURE [PartDesign::CoordinateSystem] Local_CS317  label="LCS_Frame_F_CollPoint"
  AttacherType = Attacher::AttachEngine3D
  MapMode = 5
  Support = -> [XY_Plane051]
FEATURE [PartDesign::CoordinateSystem] Local_CS320  label="LCS_Frame_Pivot"
  AttacherType = Attacher::AttachEngine3D
  AttachmentOffset = pos=(0,64,145) rot=(0,0,1;0rad)
  MapMode = 5
  Placement = pos=(0,64,145) rot=(0,0,1;0rad)
  Support = -> [XY_Plane051]
  expr: .AttachmentOffset.Base.y = <<Common>>#<<Parameters>>.cpointpos
  expr: .AttachmentOffset.Base.z = <<Common>>#<<Parameters>>.datum_rocker_z - <<Common>>#<<Parameters>>.datum_lowercell
FEATURE [PartDesign::Body] Body037  label="Frame_F"
  BaseFeature = -> Pad024
  Group = -> [Clone008,DatumPlane012,Sketch059,Hole029,Local_CS089,Local_CS092,Local_CS317,Local_CS320]
  Origin = -> Origin051
  Placement = pos=(0,-64,-62) rot=(0,0,1;0rad)
  Tip = -> Hole029
  expr: .Placement.Base.y = -<<Common>>#<<Parameters>>.cpointpos
  expr: .Placement.Base.z = <<Common>>#<<Parameters>>.datum_uppercell - <<Common>>#<<Parameters>>.pri_cellfloat - 10
PROVENANCE & LICENSES
A FreeCAD (.FCStd) document from a public repository crawl; recipes are the document's own serialized feature recipes (and, for linked parts, companion documents' recipes).
License: as declared in the source repository (recorded in the dataset sidecar).
